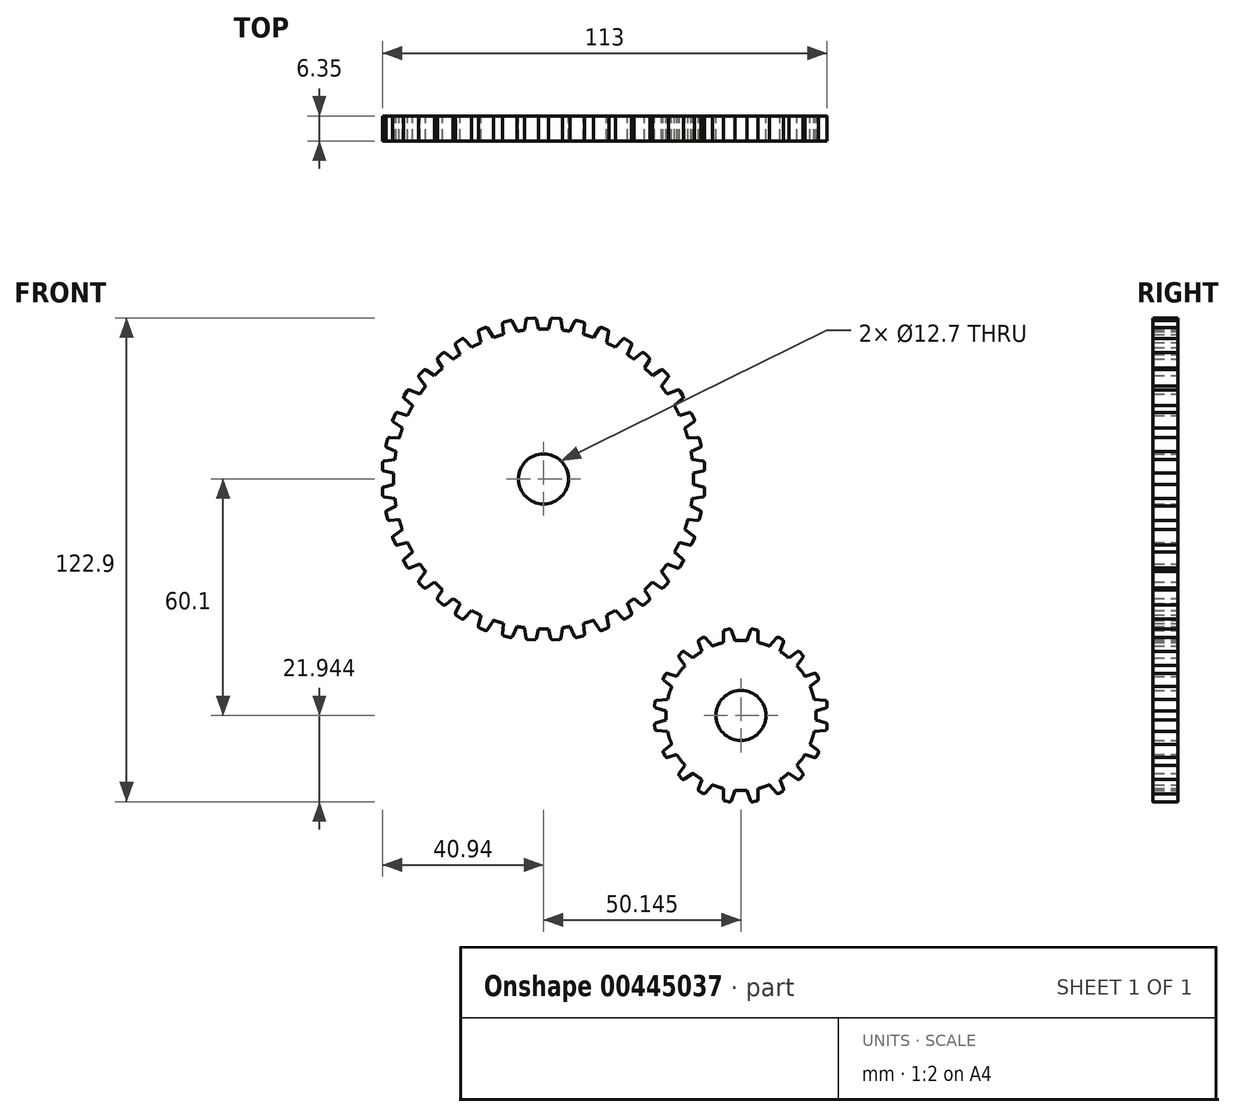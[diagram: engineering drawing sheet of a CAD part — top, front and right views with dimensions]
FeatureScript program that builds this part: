
annotation { "Feature Type Name" : "Feature", "Feature Type Description" : "" }
export const myFeature = defineFeature(function(context is Context, id is Id, definition is map)
    precondition{}
    {
        {
            var Q0;
            Q0=qCreatedBy(makeId("Front.planeOp"),FACE);
            var sketch = newSketch(context, id + "F0", { "sketchPlane" : qUnion([Q0])});
            skCircle(sketch, "E0", {"center": v(-27.1, 27.65) * mm, "radius": 38.1 * mm});
            skCircle(sketch, "E1", {"center": v(-27.1, 27.65) * mm, "radius": 6.35 * mm});
            skLineSegment(sketch, "E2", {"start": v(10.04, 32.06) * mm, "end": v(10.15, 29.52) * mm});
            skLineSegment(sketch, "E3", {"start": v(13.33, 32.24) * mm, "end": v(10.6, 32.59) * mm});
            skLineSegment(sketch, "E4", {"start": v(10.77, 29.05) * mm, "end": v(13.45, 29.65) * mm});
            skLineSegment(sketch, "E5", {"start": v(13.77, 31.76) * mm, "end": v(13.84, 30.17) * mm});
            skPoint(sketch, "E6.visualSharp", {"position": v(13.75, 32.18) * mm});
            skArc(sketch, "E6.filletArc", {"start": v(13.77, 31.76) * mm, "mid": v(13.64, 32.08) * mm, "end": v(13.33, 32.24) * mm});
            skPoint(sketch, "E7.visualSharp", {"position": v(10, 32.67) * mm});
            skArc(sketch, "E7.filletArc", {"start": v(10.6, 32.59) * mm, "mid": v(10.2, 32.46) * mm, "end": v(10.04, 32.06) * mm});
            skArc(sketch, "E8.filletArc", {"start": v(10.15, 29.52) * mm, "mid": v(10.35, 29.14) * mm, "end": v(10.77, 29.05) * mm});
            skPoint(sketch, "E9.visualSharp", {"position": v(13.86, 29.75) * mm});
            skArc(sketch, "E9.filletArc", {"start": v(13.45, 29.65) * mm, "mid": v(13.74, 29.84) * mm, "end": v(13.84, 30.17) * mm});
            skLineSegment(sketch, "E10.0", {"start": v(13.86, 29.75) * mm, "end": v(13.75, 32.18) * mm, "construction": true});
            skLineSegment(sketch, "E11", {"start": v(6.96, 43.07) * mm, "end": v(8.03, 40.77) * mm});
            skLineSegment(sketch, "E12", {"start": v(9.93, 44.48) * mm, "end": v(7.28, 43.77) * mm});
            skLineSegment(sketch, "E13", {"start": v(8.78, 40.57) * mm, "end": v(11.03, 42.14) * mm});
            skLineSegment(sketch, "E14", {"start": v(10.52, 44.2) * mm, "end": v(11.2, 42.77) * mm});
            skPoint(sketch, "E15.visualSharp", {"position": v(10.34, 44.6) * mm});
            skArc(sketch, "E15.filletArc", {"start": v(10.52, 44.2) * mm, "mid": v(10.28, 44.45) * mm, "end": v(9.93, 44.48) * mm});
            skPoint(sketch, "E16.visualSharp", {"position": v(6.7, 43.62) * mm});
            skArc(sketch, "E16.filletArc", {"start": v(7.28, 43.77) * mm, "mid": v(6.96, 43.5) * mm, "end": v(6.96, 43.07) * mm});
            skPoint(sketch, "E17.visualSharp", {"position": v(8.29, 40.22) * mm});
            skArc(sketch, "E17.filletArc", {"start": v(8.03, 40.77) * mm, "mid": v(8.36, 40.5) * mm, "end": v(8.78, 40.57) * mm});
            skPoint(sketch, "E18.visualSharp", {"position": v(11.38, 42.38) * mm});
            skArc(sketch, "E18.filletArc", {"start": v(11.03, 42.14) * mm, "mid": v(11.23, 42.42) * mm, "end": v(11.2, 42.77) * mm});
            skLineSegment(sketch, "E19.0", {"start": v(11.38, 42.38) * mm, "end": v(10.34, 44.6) * mm, "construction": true});
            skLineSegment(sketch, "E20", {"start": v(4.05, 48.5) * mm, "end": v(5.33, 46.32) * mm});
            skLineSegment(sketch, "E21", {"start": v(6.97, 50.23) * mm, "end": v(4.3, 49.24) * mm});
            skLineSegment(sketch, "E22", {"start": v(6.1, 46.19) * mm, "end": v(8.26, 48.02) * mm});
            skLineSegment(sketch, "E23", {"start": v(7.58, 50) * mm, "end": v(8.37, 48.67) * mm});
            skPoint(sketch, "E24.visualSharp", {"position": v(7.37, 50.38) * mm});
            skArc(sketch, "E24.filletArc", {"start": v(7.58, 50) * mm, "mid": v(7.32, 50.23) * mm, "end": v(6.97, 50.23) * mm});
            skPoint(sketch, "E25.visualSharp", {"position": v(3.74, 49.03) * mm});
            skArc(sketch, "E25.filletArc", {"start": v(4.3, 49.24) * mm, "mid": v(4, 48.94) * mm, "end": v(4.05, 48.5) * mm});
            skPoint(sketch, "E26.visualSharp", {"position": v(5.63, 45.8) * mm});
            skArc(sketch, "E26.filletArc", {"start": v(5.33, 46.32) * mm, "mid": v(5.68, 46.07) * mm, "end": v(6.1, 46.19) * mm});
            skPoint(sketch, "E27.visualSharp", {"position": v(8.58, 48.3) * mm});
            skArc(sketch, "E27.filletArc", {"start": v(8.26, 48.02) * mm, "mid": v(8.43, 48.32) * mm, "end": v(8.37, 48.67) * mm});
            skLineSegment(sketch, "E28.0", {"start": v(8.58, 48.3) * mm, "end": v(7.37, 50.38) * mm, "construction": true});
            skLineSegment(sketch, "E29", {"start": v(0.34, 53.06) * mm, "end": v(2.06, 51.19) * mm});
            skLineSegment(sketch, "E30", {"start": v(2.75, 55.3) * mm, "end": v(0.44, 53.83) * mm});
            skLineSegment(sketch, "E31", {"start": v(2.84, 51.22) * mm, "end": v(4.5, 53.4) * mm});
            skLineSegment(sketch, "E32", {"start": v(3.4, 55.22) * mm, "end": v(4.47, 54.06) * mm});
            skPoint(sketch, "E33.visualSharp", {"position": v(3.1, 55.54) * mm});
            skArc(sketch, "E33.filletArc", {"start": v(3.4, 55.22) * mm, "mid": v(3.09, 55.38) * mm, "end": v(2.75, 55.3) * mm});
            skPoint(sketch, "E34.visualSharp", {"position": v(-0.07, 53.5) * mm});
            skArc(sketch, "E34.filletArc", {"start": v(0.44, 53.83) * mm, "mid": v(0.2, 53.47) * mm, "end": v(0.34, 53.06) * mm});
            skPoint(sketch, "E35.visualSharp", {"position": v(2.47, 50.74) * mm});
            skArc(sketch, "E35.filletArc", {"start": v(2.06, 51.19) * mm, "mid": v(2.46, 51.03) * mm, "end": v(2.84, 51.22) * mm});
            skPoint(sketch, "E36.visualSharp", {"position": v(4.76, 53.74) * mm});
            skArc(sketch, "E36.filletArc", {"start": v(4.5, 53.4) * mm, "mid": v(4.6, 53.74) * mm, "end": v(4.47, 54.06) * mm});
            skLineSegment(sketch, "E37.0", {"start": v(4.76, 53.74) * mm, "end": v(3.1, 55.54) * mm, "construction": true});
            skLineSegment(sketch, "E38", {"start": v(-8.73, 60.35) * mm, "end": v(-6.6, 58.97) * mm});
            skLineSegment(sketch, "E39", {"start": v(-6.96, 63.13) * mm, "end": v(-8.82, 61.12) * mm});
            skLineSegment(sketch, "E40", {"start": v(-5.85, 59.2) * mm, "end": v(-4.79, 61.73) * mm});
            skLineSegment(sketch, "E41", {"start": v(-6.31, 63.21) * mm, "end": v(-4.98, 62.35) * mm});
            skPoint(sketch, "E42.visualSharp", {"position": v(-6.67, 63.44) * mm});
            skArc(sketch, "E42.filletArc", {"start": v(-6.31, 63.21) * mm, "mid": v(-6.65, 63.29) * mm, "end": v(-6.96, 63.13) * mm});
            skPoint(sketch, "E43.visualSharp", {"position": v(-9.24, 60.68) * mm});
            skArc(sketch, "E43.filletArc", {"start": v(-8.82, 61.12) * mm, "mid": v(-8.96, 60.71) * mm, "end": v(-8.73, 60.35) * mm});
            skPoint(sketch, "E44.visualSharp", {"position": v(-6.09, 58.64) * mm});
            skArc(sketch, "E44.filletArc", {"start": v(-6.6, 58.97) * mm, "mid": v(-6.17, 58.91) * mm, "end": v(-5.85, 59.2) * mm});
            skPoint(sketch, "E45.visualSharp", {"position": v(-4.62, 62.12) * mm});
            skArc(sketch, "E45.filletArc", {"start": v(-4.79, 61.73) * mm, "mid": v(-4.77, 62.07) * mm, "end": v(-4.98, 62.35) * mm});
            skLineSegment(sketch, "E46.0", {"start": v(-4.62, 62.12) * mm, "end": v(-6.67, 63.44) * mm, "construction": true});
            skLineSegment(sketch, "E47", {"start": v(-14.2, 62.88) * mm, "end": v(-11.86, 61.89) * mm});
            skLineSegment(sketch, "E48", {"start": v(-12.92, 65.94) * mm, "end": v(-14.42, 63.62) * mm});
            skLineSegment(sketch, "E49", {"start": v(-11.16, 62.24) * mm, "end": v(-10.54, 64.93) * mm});
            skLineSegment(sketch, "E50", {"start": v(-12.3, 66.13) * mm, "end": v(-10.84, 65.51) * mm});
            skPoint(sketch, "E51.visualSharp", {"position": v(-12.69, 66.3) * mm});
            skArc(sketch, "E51.filletArc", {"start": v(-12.3, 66.13) * mm, "mid": v(-12.64, 66.15) * mm, "end": v(-12.92, 65.94) * mm});
            skPoint(sketch, "E52.visualSharp", {"position": v(-14.75, 63.12) * mm});
            skArc(sketch, "E52.filletArc", {"start": v(-14.42, 63.62) * mm, "mid": v(-14.48, 63.2) * mm, "end": v(-14.2, 62.88) * mm});
            skPoint(sketch, "E53.visualSharp", {"position": v(-11.3, 61.65) * mm});
            skArc(sketch, "E53.filletArc", {"start": v(-11.86, 61.89) * mm, "mid": v(-11.43, 61.9) * mm, "end": v(-11.16, 62.24) * mm});
            skPoint(sketch, "E54.visualSharp", {"position": v(-10.45, 65.34) * mm});
            skArc(sketch, "E54.filletArc", {"start": v(-10.54, 64.93) * mm, "mid": v(-10.59, 65.27) * mm, "end": v(-10.84, 65.51) * mm});
            skLineSegment(sketch, "E55.0", {"start": v(-10.45, 65.34) * mm, "end": v(-12.69, 66.3) * mm, "construction": true});
            skLineSegment(sketch, "E56", {"start": v(-20.02, 64.46) * mm, "end": v(-17.57, 63.8) * mm});
            skLineSegment(sketch, "E57", {"start": v(-19.2, 67.65) * mm, "end": v(-20.35, 65.17) * mm});
            skLineSegment(sketch, "E58", {"start": v(-16.93, 64.25) * mm, "end": v(-16.7, 66.98) * mm});
            skLineSegment(sketch, "E59", {"start": v(-18.6, 67.93) * mm, "end": v(-17.07, 67.52) * mm});
            skPoint(sketch, "E60.visualSharp", {"position": v(-19.02, 68.04) * mm});
            skArc(sketch, "E60.filletArc", {"start": v(-18.6, 67.93) * mm, "mid": v(-18.95, 67.9) * mm, "end": v(-19.2, 67.65) * mm});
            skPoint(sketch, "E61.visualSharp", {"position": v(-20.6, 64.62) * mm});
            skArc(sketch, "E61.filletArc", {"start": v(-20.35, 65.17) * mm, "mid": v(-20.35, 64.74) * mm, "end": v(-20.02, 64.46) * mm});
            skPoint(sketch, "E62.visualSharp", {"position": v(-16.98, 63.65) * mm});
            skArc(sketch, "E62.filletArc", {"start": v(-17.57, 63.8) * mm, "mid": v(-17.15, 63.88) * mm, "end": v(-16.93, 64.25) * mm});
            skPoint(sketch, "E63.visualSharp", {"position": v(-16.66, 67.4) * mm});
            skArc(sketch, "E63.filletArc", {"start": v(-16.7, 66.98) * mm, "mid": v(-16.79, 67.32) * mm, "end": v(-17.07, 67.52) * mm});
            skLineSegment(sketch, "E64.0", {"start": v(-16.66, 67.4) * mm, "end": v(-19.02, 68.04) * mm, "construction": true});
            skLineSegment(sketch, "E65", {"start": v(8.98, 37.34) * mm, "end": v(9.63, 34.89) * mm});
            skLineSegment(sketch, "E66", {"start": v(11.97, 38.2) * mm, "end": v(9.42, 37.98) * mm});
            skLineSegment(sketch, "E67", {"start": v(10.34, 34.56) * mm, "end": v(12.66, 35.63) * mm});
            skLineSegment(sketch, "E68", {"start": v(12.5, 37.82) * mm, "end": v(12.93, 36.22) * mm});
            skPoint(sketch, "E69.visualSharp", {"position": v(12.4, 38.23) * mm});
            skArc(sketch, "E69.filletArc", {"start": v(12.5, 37.82) * mm, "mid": v(12.3, 38.1) * mm, "end": v(11.97, 38.2) * mm});
            skPoint(sketch, "E70.visualSharp", {"position": v(8.82, 37.92) * mm});
            skArc(sketch, "E70.filletArc", {"start": v(9.42, 37.98) * mm, "mid": v(9.05, 37.76) * mm, "end": v(8.98, 37.34) * mm});
            skPoint(sketch, "E71.visualSharp", {"position": v(9.79, 34.3) * mm});
            skArc(sketch, "E71.filletArc", {"start": v(9.63, 34.89) * mm, "mid": v(9.9, 34.56) * mm, "end": v(10.34, 34.56) * mm});
            skPoint(sketch, "E72.visualSharp", {"position": v(13.04, 35.81) * mm});
            skArc(sketch, "E72.filletArc", {"start": v(12.66, 35.63) * mm, "mid": v(12.9, 35.88) * mm, "end": v(12.93, 36.22) * mm});
            skLineSegment(sketch, "E73.0", {"start": v(13.04, 35.81) * mm, "end": v(12.4, 38.23) * mm, "construction": true});
            skLineSegment(sketch, "E74", {"start": v(-25.32, 65) * mm, "end": v(-22.78, 64.91) * mm});
            skLineSegment(sketch, "E75", {"start": v(-25.27, 68.11) * mm, "end": v(-25.8, 65.6) * mm});
            skLineSegment(sketch, "E76", {"start": v(-22.26, 65.49) * mm, "end": v(-22.62, 68.02) * mm});
            skLineSegment(sketch, "E77", {"start": v(-24.76, 68.51) * mm, "end": v(-23.1, 68.46) * mm});
            skPoint(sketch, "E78.visualSharp", {"position": v(-25.18, 68.53) * mm});
            skArc(sketch, "E78.filletArc", {"start": v(-24.76, 68.51) * mm, "mid": v(-25.09, 68.4) * mm, "end": v(-25.27, 68.11) * mm});
            skPoint(sketch, "E79.visualSharp", {"position": v(-25.93, 65.02) * mm});
            skArc(sketch, "E79.filletArc", {"start": v(-25.8, 65.6) * mm, "mid": v(-25.7, 65.2) * mm, "end": v(-25.32, 65) * mm});
            skPoint(sketch, "E80.visualSharp", {"position": v(-22.18, 64.9) * mm});
            skArc(sketch, "E80.filletArc", {"start": v(-22.78, 64.91) * mm, "mid": v(-22.39, 65.08) * mm, "end": v(-22.26, 65.49) * mm});
            skPoint(sketch, "E81.visualSharp", {"position": v(-22.68, 68.44) * mm});
            skArc(sketch, "E81.filletArc", {"start": v(-22.62, 68.02) * mm, "mid": v(-22.79, 68.33) * mm, "end": v(-23.1, 68.46) * mm});
            skLineSegment(sketch, "E82.0", {"start": v(-22.68, 68.44) * mm, "end": v(-25.18, 68.53) * mm, "construction": true});
            skPoint(sketch, "E83.endSnap0", {"position": v(10.7, 38.09) * mm});
            skLineSegment(sketch, "E84", {"start": v(-27.1, 65.75) * mm, "end": v(-27.1, -10.45) * mm, "construction": true});
            skLineSegment(sketch, "E85", {"start": v(-65.2, 27.65) * mm, "end": v(11, 27.65) * mm, "construction": true});
            skLineSegment(sketch, "E86", {"start": v(-4.21, 57.29) * mm, "end": v(-2.34, 55.57) * mm});
            skLineSegment(sketch, "E87", {"start": v(-2.15, 59.62) * mm, "end": v(-4.18, 58.06) * mm});
            skLineSegment(sketch, "E88", {"start": v(-1.57, 55.68) * mm, "end": v(-0.2, 57.84) * mm});
            skLineSegment(sketch, "E89", {"start": v(-1.5, 59.6) * mm, "end": v(-0.28, 58.48) * mm});
            skPoint(sketch, "E90.visualSharp", {"position": v(-1.82, 59.88) * mm});
            skArc(sketch, "E90.filletArc", {"start": v(-1.5, 59.6) * mm, "mid": v(-1.82, 59.73) * mm, "end": v(-2.15, 59.62) * mm});
            skPoint(sketch, "E91.visualSharp", {"position": v(-4.66, 57.7) * mm});
            skArc(sketch, "E91.filletArc", {"start": v(-4.18, 58.06) * mm, "mid": v(-4.38, 57.68) * mm, "end": v(-4.21, 57.29) * mm});
            skPoint(sketch, "E92.visualSharp", {"position": v(-1.9, 55.16) * mm});
            skArc(sketch, "E92.filletArc", {"start": v(-2.34, 55.57) * mm, "mid": v(-1.93, 55.44) * mm, "end": v(-1.57, 55.68) * mm});
            skPoint(sketch, "E93.visualSharp", {"position": v(0.03, 58.2) * mm});
            skArc(sketch, "E93.filletArc", {"start": v(-0.2, 57.84) * mm, "mid": v(-0.12, 58.17) * mm, "end": v(-0.28, 58.48) * mm});
            skLineSegment(sketch, "E94.0", {"start": v(0.03, 58.2) * mm, "end": v(-1.82, 59.88) * mm, "construction": true});
            skLineSegment(sketch, "E95.MirrorCS", {"start": v(-57.6, 55.22) * mm, "end": v(-58.67, 54.06) * mm});
            skArc(sketch, "E96.MirrorCS", {"start": v(-29.44, 68.51) * mm, "mid": v(-29.11, 68.4) * mm, "end": v(-28.93, 68.11) * mm});
            skArc(sketch, "E97.MirrorCS", {"start": v(-37.5, 66.98) * mm, "mid": v(-37.41, 67.32) * mm, "end": v(-37.13, 67.52) * mm});
            skLineSegment(sketch, "E98.MirrorCS", {"start": v(-61.78, 50) * mm, "end": v(-62.57, 48.67) * mm});
            skArc(sketch, "E99.MirrorCS", {"start": v(-66.7, 37.82) * mm, "mid": v(-66.5, 38.1) * mm, "end": v(-66.17, 38.2) * mm});
            skArc(sketch, "E100.MirrorCS", {"start": v(-43.66, 64.93) * mm, "mid": v(-43.61, 65.27) * mm, "end": v(-43.36, 65.51) * mm});
            skArc(sketch, "E101.MirrorCS", {"start": v(-63.62, 37.98) * mm, "mid": v(-63.25, 37.76) * mm, "end": v(-63.18, 37.34) * mm});
            skArc(sketch, "E102.MirrorCS", {"start": v(-33.85, 65.17) * mm, "mid": v(-33.85, 64.74) * mm, "end": v(-34.18, 64.46) * mm});
            skArc(sketch, "E103.MirrorCS", {"start": v(-49.42, 61.73) * mm, "mid": v(-49.43, 62.07) * mm, "end": v(-49.22, 62.35) * mm});
            skArc(sketch, "E104.MirrorCS", {"start": v(-64.8, 32.59) * mm, "mid": v(-64.4, 32.46) * mm, "end": v(-64.24, 32.06) * mm});
            skArc(sketch, "E105.MirrorCS", {"start": v(-50.02, 58.06) * mm, "mid": v(-49.82, 57.68) * mm, "end": v(-49.99, 57.29) * mm});
            skArc(sketch, "E106.MirrorCS", {"start": v(-66.86, 35.63) * mm, "mid": v(-67.1, 35.88) * mm, "end": v(-67.13, 36.22) * mm});
            skArc(sketch, "E107.MirrorCS", {"start": v(-54.64, 53.83) * mm, "mid": v(-54.4, 53.47) * mm, "end": v(-54.54, 53.06) * mm});
            skLineSegment(sketch, "E108.MirrorCS", {"start": v(-49.58, 62.12) * mm, "end": v(-47.53, 63.44) * mm, "construction": true});
            skArc(sketch, "E109.MirrorCS", {"start": v(-31.58, 68.02) * mm, "mid": v(-31.41, 68.33) * mm, "end": v(-31.1, 68.46) * mm});
            skArc(sketch, "E110.MirrorCS", {"start": v(-36.63, 63.8) * mm, "mid": v(-37.05, 63.88) * mm, "end": v(-37.27, 64.25) * mm});
            skArc(sketch, "E111.MirrorCS", {"start": v(-62.23, 40.77) * mm, "mid": v(-62.56, 40.5) * mm, "end": v(-62.98, 40.57) * mm});
            skLineSegment(sketch, "E112.MirrorCS", {"start": v(-43.75, 65.34) * mm, "end": v(-41.51, 66.3) * mm, "construction": true});
            skArc(sketch, "E113.MirrorCS", {"start": v(-39.78, 63.62) * mm, "mid": v(-39.72, 63.2) * mm, "end": v(-40, 62.88) * mm});
            skArc(sketch, "E114.MirrorCS", {"start": v(-31.42, 64.91) * mm, "mid": v(-31.81, 65.08) * mm, "end": v(-31.94, 65.49) * mm});
            skArc(sketch, "E115.MirrorCS", {"start": v(-62.46, 48.02) * mm, "mid": v(-62.63, 48.32) * mm, "end": v(-62.57, 48.67) * mm});
            skArc(sketch, "E116.MirrorCS", {"start": v(-64.35, 29.52) * mm, "mid": v(-64.55, 29.14) * mm, "end": v(-64.97, 29.05) * mm});
            skLineSegment(sketch, "E117.MirrorCS", {"start": v(-41.9, 66.13) * mm, "end": v(-43.36, 65.51) * mm});
            skArc(sketch, "E118.MirrorCS", {"start": v(-58.5, 49.24) * mm, "mid": v(-58.2, 48.94) * mm, "end": v(-58.25, 48.5) * mm});
            skArc(sketch, "E119.MirrorCS", {"start": v(-47.6, 58.97) * mm, "mid": v(-48.03, 58.91) * mm, "end": v(-48.35, 59.2) * mm});
            skArc(sketch, "E120.MirrorCS", {"start": v(-35.6, 67.93) * mm, "mid": v(-35.25, 67.9) * mm, "end": v(-35, 67.65) * mm});
            skLineSegment(sketch, "E121.MirrorCS", {"start": v(-47.89, 63.21) * mm, "end": v(-49.22, 62.35) * mm});
            skArc(sketch, "E122.MirrorCS", {"start": v(-67.97, 31.76) * mm, "mid": v(-67.84, 32.08) * mm, "end": v(-67.53, 32.24) * mm});
            skArc(sketch, "E123.MirrorCS", {"start": v(-59.53, 46.32) * mm, "mid": v(-59.88, 46.07) * mm, "end": v(-60.3, 46.19) * mm});
            skArc(sketch, "E124.MirrorCS", {"start": v(-47.89, 63.21) * mm, "mid": v(-47.55, 63.29) * mm, "end": v(-47.24, 63.13) * mm});
            skLineSegment(sketch, "E125.MirrorCS", {"start": v(-58.96, 53.74) * mm, "end": v(-57.3, 55.54) * mm, "construction": true});
            skArc(sketch, "E126.MirrorCS", {"start": v(-63.83, 34.89) * mm, "mid": v(-64.1, 34.56) * mm, "end": v(-64.54, 34.56) * mm});
            skLineSegment(sketch, "E127.MirrorCS", {"start": v(-62.78, 48.3) * mm, "end": v(-61.57, 50.38) * mm, "construction": true});
            skArc(sketch, "E128.MirrorCS", {"start": v(-51.86, 55.57) * mm, "mid": v(-52.27, 55.44) * mm, "end": v(-52.63, 55.68) * mm});
            skArc(sketch, "E129.MirrorCS", {"start": v(-64.73, 44.2) * mm, "mid": v(-64.48, 44.45) * mm, "end": v(-64.13, 44.48) * mm});
            skArc(sketch, "E130.MirrorCS", {"start": v(-54, 57.84) * mm, "mid": v(-54.08, 58.17) * mm, "end": v(-53.92, 58.48) * mm});
            skArc(sketch, "E131.MirrorCS", {"start": v(-61.78, 50) * mm, "mid": v(-61.52, 50.23) * mm, "end": v(-61.17, 50.23) * mm});
            skArc(sketch, "E132.MirrorCS", {"start": v(-45.38, 61.12) * mm, "mid": v(-45.24, 60.71) * mm, "end": v(-45.47, 60.35) * mm});
            skArc(sketch, "E133.MirrorCS", {"start": v(-58.7, 53.4) * mm, "mid": v(-58.8, 53.74) * mm, "end": v(-58.67, 54.06) * mm});
            skArc(sketch, "E134.MirrorCS", {"start": v(-52.7, 59.6) * mm, "mid": v(-52.38, 59.73) * mm, "end": v(-52.05, 59.62) * mm});
            skArc(sketch, "E135.MirrorCS", {"start": v(-56.26, 51.19) * mm, "mid": v(-56.66, 51.03) * mm, "end": v(-57.04, 51.22) * mm});
            skArc(sketch, "E136.MirrorCS", {"start": v(-42.34, 61.89) * mm, "mid": v(-42.77, 61.9) * mm, "end": v(-43.04, 62.24) * mm});
            skArc(sketch, "E137.MirrorCS", {"start": v(-65.23, 42.14) * mm, "mid": v(-65.43, 42.42) * mm, "end": v(-65.4, 42.77) * mm});
            skArc(sketch, "E138.MirrorCS", {"start": v(-57.6, 55.22) * mm, "mid": v(-57.29, 55.38) * mm, "end": v(-56.95, 55.3) * mm});
            skArc(sketch, "E139.MirrorCS", {"start": v(-61.49, 43.77) * mm, "mid": v(-61.16, 43.5) * mm, "end": v(-61.16, 43.07) * mm});
            skArc(sketch, "E140.MirrorCS", {"start": v(-28.4, 65.6) * mm, "mid": v(-28.5, 65.2) * mm, "end": v(-28.88, 65) * mm});
            skArc(sketch, "E141.MirrorCS", {"start": v(-41.9, 66.13) * mm, "mid": v(-41.56, 66.15) * mm, "end": v(-41.28, 65.94) * mm});
            skLineSegment(sketch, "E142.MirrorCS", {"start": v(-29.44, 68.51) * mm, "end": v(-31.1, 68.46) * mm});
            skLineSegment(sketch, "E143.MirrorCS", {"start": v(-52.7, 59.6) * mm, "end": v(-53.92, 58.48) * mm});
            skLineSegment(sketch, "E144.MirrorCS", {"start": v(-64.73, 44.2) * mm, "end": v(-65.4, 42.77) * mm});
            skLineSegment(sketch, "E145.MirrorCS", {"start": v(-66.7, 37.82) * mm, "end": v(-67.13, 36.22) * mm});
            skLineSegment(sketch, "E146.MirrorCS", {"start": v(-35.6, 67.93) * mm, "end": v(-37.13, 67.52) * mm});
            skLineSegment(sketch, "E147.MirrorCS", {"start": v(-66.17, 38.2) * mm, "end": v(-63.62, 37.98) * mm});
            skArc(sketch, "E148.MirrorCS", {"start": v(-67.65, 29.65) * mm, "mid": v(-67.94, 29.84) * mm, "end": v(-68.04, 30.17) * mm});
            skLineSegment(sketch, "E149.MirrorCS", {"start": v(-54.23, 58.2) * mm, "end": v(-52.38, 59.88) * mm, "construction": true});
            skLineSegment(sketch, "E150.MirrorCS", {"start": v(-28.88, 65) * mm, "end": v(-31.42, 64.91) * mm});
            skLineSegment(sketch, "E151.MirrorCS", {"start": v(-37.54, 67.4) * mm, "end": v(-35.18, 68.04) * mm, "construction": true});
            skLineSegment(sketch, "E152.MirrorCS", {"start": v(-31.52, 68.44) * mm, "end": v(-29.02, 68.53) * mm, "construction": true});
            skLineSegment(sketch, "E153.MirrorCS", {"start": v(-61.16, 43.07) * mm, "end": v(-62.23, 40.77) * mm});
            skLineSegment(sketch, "E154.MirrorCS", {"start": v(-67.97, 31.76) * mm, "end": v(-68.04, 30.17) * mm});
            skLineSegment(sketch, "E155.MirrorCS", {"start": v(-67.24, 35.81) * mm, "end": v(-66.6, 38.23) * mm, "construction": true});
            skLineSegment(sketch, "E156.MirrorCS", {"start": v(-40, 62.88) * mm, "end": v(-42.34, 61.89) * mm});
            skLineSegment(sketch, "E157.MirrorCS", {"start": v(-65.58, 42.38) * mm, "end": v(-64.55, 44.6) * mm, "construction": true});
            skLineSegment(sketch, "E158.MirrorCS", {"start": v(-34.18, 64.46) * mm, "end": v(-36.63, 63.8) * mm});
            skLineSegment(sketch, "E159.MirrorCS", {"start": v(-52.05, 59.62) * mm, "end": v(-50.02, 58.06) * mm});
            skPoint(sketch, "E160.MirrorP", {"position": v(-52.38, 59.88) * mm});
            skPoint(sketch, "E161.MirrorP", {"position": v(-47.53, 63.44) * mm});
            skLineSegment(sketch, "E162.MirrorCS", {"start": v(-52.63, 55.68) * mm, "end": v(-54, 57.84) * mm});
            skLineSegment(sketch, "E163.MirrorCS", {"start": v(-60.3, 46.19) * mm, "end": v(-62.46, 48.02) * mm});
            skPoint(sketch, "E164.MirrorP", {"position": v(-67.24, 35.81) * mm});
            skLineSegment(sketch, "E165.MirrorCS", {"start": v(-41.28, 65.94) * mm, "end": v(-39.78, 63.62) * mm});
            skPoint(sketch, "E166.MirrorP", {"position": v(-49.58, 62.12) * mm});
            skPoint(sketch, "E167.MirrorP", {"position": v(-62.78, 48.3) * mm});
            skLineSegment(sketch, "E168.MirrorCS", {"start": v(-54.54, 53.06) * mm, "end": v(-56.26, 51.19) * mm});
            skPoint(sketch, "E169.MirrorP", {"position": v(-31.52, 68.44) * mm});
            skPoint(sketch, "E170.MirrorP", {"position": v(-37.54, 67.4) * mm});
            skLineSegment(sketch, "E171.MirrorCS", {"start": v(-43.04, 62.24) * mm, "end": v(-43.66, 64.93) * mm});
            skLineSegment(sketch, "E172.MirrorCS", {"start": v(-37.27, 64.25) * mm, "end": v(-37.5, 66.98) * mm});
            skPoint(sketch, "E173.MirrorP", {"position": v(-37.22, 63.65) * mm});
            skLineSegment(sketch, "E174.MirrorCS", {"start": v(-56.95, 55.3) * mm, "end": v(-54.64, 53.83) * mm});
            skPoint(sketch, "E175.MirrorP", {"position": v(-64.55, 44.6) * mm});
            skPoint(sketch, "E176.MirrorP", {"position": v(-58.96, 53.74) * mm});
            skLineSegment(sketch, "E177.MirrorCS", {"start": v(-64.97, 29.05) * mm, "end": v(-67.65, 29.65) * mm});
            skLineSegment(sketch, "E178.MirrorCS", {"start": v(-31.94, 65.49) * mm, "end": v(-31.58, 68.02) * mm});
            skPoint(sketch, "E179.MirrorP", {"position": v(-63.02, 37.92) * mm});
            skPoint(sketch, "E180.MirrorP", {"position": v(-57.94, 49.03) * mm});
            skLineSegment(sketch, "E181.MirrorCS", {"start": v(-63.18, 37.34) * mm, "end": v(-63.83, 34.89) * mm});
            skLineSegment(sketch, "E182.MirrorCS", {"start": v(-62.98, 40.57) * mm, "end": v(-65.23, 42.14) * mm});
            skLineSegment(sketch, "E183.MirrorCS", {"start": v(-67.53, 32.24) * mm, "end": v(-64.8, 32.59) * mm});
            skLineSegment(sketch, "E184.MirrorCS", {"start": v(-57.04, 51.22) * mm, "end": v(-58.7, 53.4) * mm});
            skPoint(sketch, "E185.MirrorP", {"position": v(-52.3, 55.16) * mm});
            skPoint(sketch, "E186.MirrorP", {"position": v(-32.02, 64.9) * mm});
            skLineSegment(sketch, "E187.MirrorCS", {"start": v(-64.54, 34.56) * mm, "end": v(-66.86, 35.63) * mm});
            skPoint(sketch, "E188.MirrorP", {"position": v(-59.83, 45.8) * mm});
            skLineSegment(sketch, "E189.MirrorCS", {"start": v(-64.24, 32.06) * mm, "end": v(-64.35, 29.52) * mm});
            skPoint(sketch, "E190.MirrorP", {"position": v(-39.45, 63.12) * mm});
            skPoint(sketch, "E191.MirrorP", {"position": v(-61.57, 50.38) * mm});
            skPoint(sketch, "E192.MirrorP", {"position": v(-48.12, 58.64) * mm});
            skPoint(sketch, "E193.MirrorP", {"position": v(-64.9, 38.09) * mm});
            skPoint(sketch, "E194.MirrorP", {"position": v(-49.54, 57.7) * mm});
            skPoint(sketch, "E195.MirrorP", {"position": v(-66.6, 38.23) * mm});
            skPoint(sketch, "E196.MirrorP", {"position": v(-54.13, 53.5) * mm});
            skPoint(sketch, "E197.MirrorP", {"position": v(-54.23, 58.2) * mm});
            skPoint(sketch, "E198.MirrorP", {"position": v(-60.9, 43.62) * mm});
            skPoint(sketch, "E199.MirrorP", {"position": v(-64.2, 32.67) * mm});
            skLineSegment(sketch, "E200.MirrorCS", {"start": v(-28.93, 68.11) * mm, "end": v(-28.4, 65.6) * mm});
            skPoint(sketch, "E201.MirrorP", {"position": v(-33.6, 64.62) * mm});
            skLineSegment(sketch, "E202.MirrorCS", {"start": v(-45.47, 60.35) * mm, "end": v(-47.6, 58.97) * mm});
            skLineSegment(sketch, "E203.MirrorCS", {"start": v(-68.06, 29.75) * mm, "end": v(-67.95, 32.18) * mm, "construction": true});
            skPoint(sketch, "E204.MirrorP", {"position": v(-28.27, 65.02) * mm});
            skLineSegment(sketch, "E205.MirrorCS", {"start": v(-64.13, 44.48) * mm, "end": v(-61.49, 43.77) * mm});
            skLineSegment(sketch, "E206.MirrorCS", {"start": v(-35, 67.65) * mm, "end": v(-33.85, 65.17) * mm});
            skPoint(sketch, "E207.MirrorP", {"position": v(-44.96, 60.68) * mm});
            skLineSegment(sketch, "E208.MirrorCS", {"start": v(-47.24, 63.13) * mm, "end": v(-45.38, 61.12) * mm});
            skLineSegment(sketch, "E209.MirrorCS", {"start": v(-61.17, 50.23) * mm, "end": v(-58.5, 49.24) * mm});
            skLineSegment(sketch, "E210.MirrorCS", {"start": v(-49.99, 57.29) * mm, "end": v(-51.86, 55.57) * mm});
            skPoint(sketch, "E211.MirrorP", {"position": v(-63.99, 34.3) * mm});
            skPoint(sketch, "E212.MirrorP", {"position": v(-35.18, 68.04) * mm});
            skLineSegment(sketch, "E213.MirrorCS", {"start": v(-48.35, 59.2) * mm, "end": v(-49.42, 61.73) * mm});
            skPoint(sketch, "E214.MirrorP", {"position": v(-29.02, 68.53) * mm});
            skPoint(sketch, "E215.MirrorP", {"position": v(-65.58, 42.38) * mm});
            skPoint(sketch, "E216.MirrorP", {"position": v(-56.67, 50.74) * mm});
            skPoint(sketch, "E217.MirrorP", {"position": v(-42.9, 61.65) * mm});
            skPoint(sketch, "E218.MirrorP", {"position": v(-41.51, 66.3) * mm});
            skPoint(sketch, "E219.MirrorP", {"position": v(-57.3, 55.54) * mm});
            skPoint(sketch, "E220.MirrorP", {"position": v(-62.49, 40.22) * mm});
            skPoint(sketch, "E221.MirrorP", {"position": v(-43.75, 65.34) * mm});
            skLineSegment(sketch, "E222.MirrorCS", {"start": v(-58.25, 48.5) * mm, "end": v(-59.53, 46.32) * mm});
            skPoint(sketch, "E223.MirrorP", {"position": v(-68.06, 29.75) * mm});
            skPoint(sketch, "E224.MirrorP", {"position": v(-67.95, 32.18) * mm});
            skLineSegment(sketch, "E225.MirrorCS", {"start": v(11, 27.65) * mm, "end": v(-65.2, 27.65) * mm, "construction": true});
            skLineSegment(sketch, "E226.MirrorCS", {"start": v(3.4, 0.08) * mm, "end": v(4.47, 1.25) * mm});
            skLineSegment(sketch, "E227.MirrorCS", {"start": v(-18.6, -12.62) * mm, "end": v(-17.07, -12.21) * mm});
            skLineSegment(sketch, "E228.MirrorCS", {"start": v(7.58, 5.3) * mm, "end": v(8.37, 6.64) * mm});
            skLineSegment(sketch, "E229.MirrorCS", {"start": v(-52.7, -4.29) * mm, "end": v(-53.92, -3.18) * mm});
            skArc(sketch, "E230.MirrorCS", {"start": v(7.58, 5.3) * mm, "mid": v(7.32, 5.08) * mm, "end": v(6.97, 5.08) * mm});
            skArc(sketch, "E231.MirrorCS", {"start": v(-12.3, -10.82) * mm, "mid": v(-12.64, -10.84) * mm, "end": v(-12.92, -10.63) * mm});
            skLineSegment(sketch, "E232.MirrorCS", {"start": v(4.76, 1.56) * mm, "end": v(3.1, -0.23) * mm, "construction": true});
            skLineSegment(sketch, "E233.MirrorCS", {"start": v(-6.31, -7.9) * mm, "end": v(-4.98, -7.04) * mm});
            skLineSegment(sketch, "E234.MirrorCS", {"start": v(12.5, 17.49) * mm, "end": v(12.93, 19.08) * mm});
            skArc(sketch, "E235.MirrorCS", {"start": v(4.5, 1.9) * mm, "mid": v(4.6, 1.57) * mm, "end": v(4.47, 1.25) * mm});
            skArc(sketch, "E236.MirrorCS", {"start": v(3.4, 0.08) * mm, "mid": v(3.09, -0.08) * mm, "end": v(2.75, 0) * mm});
            skLineSegment(sketch, "E237.MirrorCS", {"start": v(-24.76, -13.2) * mm, "end": v(-23.1, -13.15) * mm});
            skArc(sketch, "E238.MirrorCS", {"start": v(-16.7, -11.68) * mm, "mid": v(-16.79, -12.01) * mm, "end": v(-17.07, -12.21) * mm});
            skLineSegment(sketch, "E239.MirrorCS", {"start": v(-61.78, 5.3) * mm, "end": v(-62.57, 6.64) * mm});
            skArc(sketch, "E240.MirrorCS", {"start": v(-18.6, -12.62) * mm, "mid": v(-18.95, -12.6) * mm, "end": v(-19.2, -12.35) * mm});
            skArc(sketch, "E241.MirrorCS", {"start": v(-24.76, -13.2) * mm, "mid": v(-25.09, -13.1) * mm, "end": v(-25.27, -12.8) * mm});
            skLineSegment(sketch, "E242.MirrorCS", {"start": v(-41.9, -10.82) * mm, "end": v(-43.36, -10.2) * mm});
            skLineSegment(sketch, "E243.MirrorCS", {"start": v(-1.5, -4.29) * mm, "end": v(-0.28, -3.18) * mm});
            skArc(sketch, "E244.MirrorCS", {"start": v(12.5, 17.49) * mm, "mid": v(12.3, 17.2) * mm, "end": v(11.97, 17.11) * mm});
            skLineSegment(sketch, "E245.MirrorCS", {"start": v(-12.3, -10.82) * mm, "end": v(-10.84, -10.2) * mm});
            skArc(sketch, "E246.MirrorCS", {"start": v(-4.79, -6.42) * mm, "mid": v(-4.77, -6.77) * mm, "end": v(-4.98, -7.04) * mm});
            skArc(sketch, "E247.MirrorCS", {"start": v(-1.5, -4.29) * mm, "mid": v(-1.82, -4.42) * mm, "end": v(-2.15, -4.32) * mm});
            skLineSegment(sketch, "E248.MirrorCS", {"start": v(-35.6, -12.62) * mm, "end": v(-37.13, -12.21) * mm});
            skLineSegment(sketch, "E249.MirrorCS", {"start": v(-66.7, 17.49) * mm, "end": v(-67.13, 19.08) * mm});
            skArc(sketch, "E250.MirrorCS", {"start": v(-56.26, 4.12) * mm, "mid": v(-56.66, 4.28) * mm, "end": v(-57.04, 4.08) * mm});
            skLineSegment(sketch, "E251.MirrorCS", {"start": v(-43.75, -10.04) * mm, "end": v(-41.51, -10.99) * mm, "construction": true});
            skLineSegment(sketch, "E252.MirrorCS", {"start": v(-29.44, -13.2) * mm, "end": v(-31.1, -13.15) * mm});
            skArc(sketch, "E253.MirrorCS", {"start": v(-45.38, -5.81) * mm, "mid": v(-45.24, -5.4) * mm, "end": v(-45.47, -5.04) * mm});
            skLineSegment(sketch, "E254.MirrorCS", {"start": v(-54.23, -2.89) * mm, "end": v(-52.38, -4.58) * mm, "construction": true});
            skArc(sketch, "E255.MirrorCS", {"start": v(-6.31, -7.9) * mm, "mid": v(-6.65, -7.98) * mm, "end": v(-6.96, -7.82) * mm});
            skArc(sketch, "E256.MirrorCS", {"start": v(-47.6, -3.66) * mm, "mid": v(-48.03, -3.6) * mm, "end": v(-48.35, -3.9) * mm});
            skArc(sketch, "E257.MirrorCS", {"start": v(-64.8, 22.72) * mm, "mid": v(-64.4, 22.85) * mm, "end": v(-64.24, 23.25) * mm});
            skArc(sketch, "E258.MirrorCS", {"start": v(5.33, 8.99) * mm, "mid": v(5.68, 9.23) * mm, "end": v(6.1, 9.12) * mm});
            skArc(sketch, "E259.MirrorCS", {"start": v(-65.23, 13.17) * mm, "mid": v(-65.43, 12.88) * mm, "end": v(-65.4, 12.54) * mm});
            skLineSegment(sketch, "E260.MirrorCS", {"start": v(-64.73, 11.1) * mm, "end": v(-65.4, 12.54) * mm});
            skArc(sketch, "E261.MirrorCS", {"start": v(-36.63, -8.5) * mm, "mid": v(-37.05, -8.57) * mm, "end": v(-37.27, -8.95) * mm});
            skArc(sketch, "E262.MirrorCS", {"start": v(-58.7, 1.9) * mm, "mid": v(-58.8, 1.57) * mm, "end": v(-58.67, 1.25) * mm});
            skArc(sketch, "E263.MirrorCS", {"start": v(-6.6, -3.66) * mm, "mid": v(-6.17, -3.6) * mm, "end": v(-5.85, -3.9) * mm});
            skArc(sketch, "E264.MirrorCS", {"start": v(-47.89, -7.9) * mm, "mid": v(-47.55, -7.98) * mm, "end": v(-47.24, -7.82) * mm});
            skLineSegment(sketch, "E265.MirrorCS", {"start": v(10.52, 11.1) * mm, "end": v(11.2, 12.54) * mm});
            skLineSegment(sketch, "E266.MirrorCS", {"start": v(-62.78, 7) * mm, "end": v(-61.57, 4.93) * mm, "construction": true});
            skArc(sketch, "E267.MirrorCS", {"start": v(-41.9, -10.82) * mm, "mid": v(-41.56, -10.84) * mm, "end": v(-41.28, -10.63) * mm});
            skLineSegment(sketch, "E268.MirrorCS", {"start": v(8.58, 7) * mm, "end": v(7.37, 4.93) * mm, "construction": true});
            skArc(sketch, "E269.MirrorCS", {"start": v(10.52, 11.1) * mm, "mid": v(10.28, 10.85) * mm, "end": v(9.93, 10.82) * mm});
            skArc(sketch, "E270.MirrorCS", {"start": v(-31.42, -9.6) * mm, "mid": v(-31.81, -9.77) * mm, "end": v(-31.94, -10.18) * mm});
            skArc(sketch, "E271.MirrorCS", {"start": v(-50.02, -2.76) * mm, "mid": v(-49.82, -2.38) * mm, "end": v(-49.99, -1.98) * mm});
            skArc(sketch, "E272.MirrorCS", {"start": v(12.66, 19.67) * mm, "mid": v(12.9, 19.43) * mm, "end": v(12.93, 19.08) * mm});
            skArc(sketch, "E273.MirrorCS", {"start": v(9.42, 17.33) * mm, "mid": v(9.05, 17.54) * mm, "end": v(8.98, 17.97) * mm});
            skArc(sketch, "E274.MirrorCS", {"start": v(-33.85, -9.86) * mm, "mid": v(-33.85, -9.43) * mm, "end": v(-34.18, -9.15) * mm});
            skArc(sketch, "E275.MirrorCS", {"start": v(-66.86, 19.67) * mm, "mid": v(-67.1, 19.43) * mm, "end": v(-67.13, 19.08) * mm});
            skArc(sketch, "E276.MirrorCS", {"start": v(0.44, 1.48) * mm, "mid": v(0.2, 1.84) * mm, "end": v(0.34, 2.25) * mm});
            skArc(sketch, "E277.MirrorCS", {"start": v(-28.4, -10.3) * mm, "mid": v(-28.5, -9.88) * mm, "end": v(-28.88, -9.69) * mm});
            skArc(sketch, "E278.MirrorCS", {"start": v(-59.53, 8.99) * mm, "mid": v(-59.88, 9.23) * mm, "end": v(-60.3, 9.12) * mm});
            skArc(sketch, "E279.MirrorCS", {"start": v(-61.78, 5.3) * mm, "mid": v(-61.52, 5.08) * mm, "end": v(-61.17, 5.08) * mm});
            skLineSegment(sketch, "E280.MirrorCS", {"start": v(-65.58, 12.92) * mm, "end": v(-64.55, 10.71) * mm, "construction": true});
            skLineSegment(sketch, "E281.MirrorCS", {"start": v(11.38, 12.92) * mm, "end": v(10.34, 10.71) * mm, "construction": true});
            skLineSegment(sketch, "E282.MirrorCS", {"start": v(-47.89, -7.9) * mm, "end": v(-49.22, -7.04) * mm});
            skArc(sketch, "E283.MirrorCS", {"start": v(-0.2, -2.53) * mm, "mid": v(-0.12, -2.87) * mm, "end": v(-0.28, -3.18) * mm});
            skArc(sketch, "E284.MirrorCS", {"start": v(-54.64, 1.48) * mm, "mid": v(-54.4, 1.84) * mm, "end": v(-54.54, 2.25) * mm});
            skLineSegment(sketch, "E285.MirrorCS", {"start": v(-31.52, -13.14) * mm, "end": v(-29.02, -13.22) * mm, "construction": true});
            skArc(sketch, "E286.MirrorCS", {"start": v(-49.42, -6.42) * mm, "mid": v(-49.43, -6.77) * mm, "end": v(-49.22, -7.04) * mm});
            skArc(sketch, "E287.MirrorCS", {"start": v(-31.58, -12.72) * mm, "mid": v(-31.41, -13.02) * mm, "end": v(-31.1, -13.15) * mm});
            skLineSegment(sketch, "E288.MirrorCS", {"start": v(-58.96, 1.56) * mm, "end": v(-57.3, -0.23) * mm, "construction": true});
            skArc(sketch, "E289.MirrorCS", {"start": v(-35.6, -12.62) * mm, "mid": v(-35.25, -12.6) * mm, "end": v(-35, -12.35) * mm});
            skLineSegment(sketch, "E290.MirrorCS", {"start": v(-37.54, -12.1) * mm, "end": v(-35.18, -12.73) * mm, "construction": true});
            skLineSegment(sketch, "E291.MirrorCS", {"start": v(-49.58, -6.81) * mm, "end": v(-47.53, -8.14) * mm, "construction": true});
            skArc(sketch, "E292.MirrorCS", {"start": v(-39.78, -8.32) * mm, "mid": v(-39.72, -7.9) * mm, "end": v(-40, -7.57) * mm});
            skArc(sketch, "E293.MirrorCS", {"start": v(9.63, 20.42) * mm, "mid": v(9.9, 20.75) * mm, "end": v(10.34, 20.75) * mm});
            skArc(sketch, "E294.MirrorCS", {"start": v(4.3, 6.06) * mm, "mid": v(4, 6.37) * mm, "end": v(4.05, 6.8) * mm});
            skArc(sketch, "E295.MirrorCS", {"start": v(-42.34, -6.58) * mm, "mid": v(-42.77, -6.6) * mm, "end": v(-43.04, -6.94) * mm});
            skArc(sketch, "E296.MirrorCS", {"start": v(-2.34, -0.27) * mm, "mid": v(-1.93, -0.14) * mm, "end": v(-1.57, -0.37) * mm});
            skArc(sketch, "E297.MirrorCS", {"start": v(-63.62, 17.33) * mm, "mid": v(-63.25, 17.54) * mm, "end": v(-63.18, 17.97) * mm});
            skLineSegment(sketch, "E298.MirrorCS", {"start": v(-10.45, -10.04) * mm, "end": v(-12.69, -10.99) * mm, "construction": true});
            skLineSegment(sketch, "E299.MirrorCS", {"start": v(-67.24, 19.5) * mm, "end": v(-66.6, 17.07) * mm, "construction": true});
            skArc(sketch, "E300.MirrorCS", {"start": v(13.77, 23.55) * mm, "mid": v(13.64, 23.23) * mm, "end": v(13.33, 23.07) * mm});
            skArc(sketch, "E301.MirrorCS", {"start": v(-64.73, 11.1) * mm, "mid": v(-64.48, 10.85) * mm, "end": v(-64.13, 10.82) * mm});
            skArc(sketch, "E302.MirrorCS", {"start": v(2.06, 4.12) * mm, "mid": v(2.46, 4.28) * mm, "end": v(2.84, 4.08) * mm});
            skArc(sketch, "E303.MirrorCS", {"start": v(-66.7, 17.49) * mm, "mid": v(-66.5, 17.2) * mm, "end": v(-66.17, 17.11) * mm});
            skArc(sketch, "E304.MirrorCS", {"start": v(-62.23, 14.54) * mm, "mid": v(-62.56, 14.82) * mm, "end": v(-62.98, 14.74) * mm});
            skArc(sketch, "E305.MirrorCS", {"start": v(-4.18, -2.76) * mm, "mid": v(-4.38, -2.38) * mm, "end": v(-4.21, -1.98) * mm});
            skLineSegment(sketch, "E306.MirrorCS", {"start": v(13.04, 19.5) * mm, "end": v(12.4, 17.07) * mm, "construction": true});
            skArc(sketch, "E307.MirrorCS", {"start": v(-17.57, -8.5) * mm, "mid": v(-17.15, -8.57) * mm, "end": v(-16.93, -8.95) * mm});
            skLineSegment(sketch, "E308.MirrorCS", {"start": v(-16.66, -12.1) * mm, "end": v(-19.02, -12.73) * mm, "construction": true});
            skArc(sketch, "E309.MirrorCS", {"start": v(7.28, 11.53) * mm, "mid": v(6.96, 11.8) * mm, "end": v(6.96, 12.24) * mm});
            skArc(sketch, "E310.MirrorCS", {"start": v(-63.83, 20.42) * mm, "mid": v(-64.1, 20.75) * mm, "end": v(-64.54, 20.75) * mm});
            skLineSegment(sketch, "E311.MirrorCS", {"start": v(-57.6, 0.08) * mm, "end": v(-58.67, 1.25) * mm});
            skArc(sketch, "E312.MirrorCS", {"start": v(-57.6, 0.08) * mm, "mid": v(-57.29, -0.08) * mm, "end": v(-56.95, 0) * mm});
            skArc(sketch, "E313.MirrorCS", {"start": v(-62.46, 7.29) * mm, "mid": v(-62.63, 6.98) * mm, "end": v(-62.57, 6.64) * mm});
            skArc(sketch, "E314.MirrorCS", {"start": v(-25.8, -10.3) * mm, "mid": v(-25.7, -9.88) * mm, "end": v(-25.32, -9.69) * mm});
            skArc(sketch, "E315.MirrorCS", {"start": v(10.15, 25.78) * mm, "mid": v(10.35, 26.16) * mm, "end": v(10.77, 26.25) * mm});
            skArc(sketch, "E316.MirrorCS", {"start": v(-14.42, -8.32) * mm, "mid": v(-14.48, -7.9) * mm, "end": v(-14.2, -7.57) * mm});
            skArc(sketch, "E317.MirrorCS", {"start": v(11.03, 13.17) * mm, "mid": v(11.23, 12.88) * mm, "end": v(11.2, 12.54) * mm});
            skArc(sketch, "E318.MirrorCS", {"start": v(-52.7, -4.29) * mm, "mid": v(-52.38, -4.42) * mm, "end": v(-52.05, -4.32) * mm});
            skArc(sketch, "E319.MirrorCS", {"start": v(-10.54, -9.62) * mm, "mid": v(-10.59, -9.97) * mm, "end": v(-10.84, -10.2) * mm});
            skArc(sketch, "E320.MirrorCS", {"start": v(8.03, 14.54) * mm, "mid": v(8.36, 14.82) * mm, "end": v(8.78, 14.74) * mm});
            skArc(sketch, "E321.MirrorCS", {"start": v(-11.86, -6.58) * mm, "mid": v(-11.43, -6.6) * mm, "end": v(-11.16, -6.94) * mm});
            skArc(sketch, "E322.MirrorCS", {"start": v(-51.86, -0.27) * mm, "mid": v(-52.27, -0.14) * mm, "end": v(-52.63, -0.37) * mm});
            skArc(sketch, "E323.MirrorCS", {"start": v(-58.5, 6.06) * mm, "mid": v(-58.2, 6.37) * mm, "end": v(-58.25, 6.8) * mm});
            skArc(sketch, "E324.MirrorCS", {"start": v(8.26, 7.29) * mm, "mid": v(8.43, 6.98) * mm, "end": v(8.37, 6.64) * mm});
            skArc(sketch, "E325.MirrorCS", {"start": v(-8.82, -5.81) * mm, "mid": v(-8.96, -5.4) * mm, "end": v(-8.73, -5.04) * mm});
            skArc(sketch, "E326.MirrorCS", {"start": v(-22.78, -9.6) * mm, "mid": v(-22.39, -9.77) * mm, "end": v(-22.26, -10.18) * mm});
            skArc(sketch, "E327.MirrorCS", {"start": v(-43.66, -9.62) * mm, "mid": v(-43.61, -9.97) * mm, "end": v(-43.36, -10.2) * mm});
            skArc(sketch, "E328.MirrorCS", {"start": v(-29.44, -13.2) * mm, "mid": v(-29.11, -13.1) * mm, "end": v(-28.93, -12.8) * mm});
            skLineSegment(sketch, "E329.MirrorCS", {"start": v(-22.68, -13.14) * mm, "end": v(-25.18, -13.22) * mm, "construction": true});
            skArc(sketch, "E330.MirrorCS", {"start": v(-64.35, 25.78) * mm, "mid": v(-64.55, 26.16) * mm, "end": v(-64.97, 26.25) * mm});
            skLineSegment(sketch, "E331.MirrorCS", {"start": v(0.03, -2.89) * mm, "end": v(-1.82, -4.58) * mm, "construction": true});
            skArc(sketch, "E332.MirrorCS", {"start": v(-54, -2.53) * mm, "mid": v(-54.08, -2.87) * mm, "end": v(-53.92, -3.18) * mm});
            skArc(sketch, "E333.MirrorCS", {"start": v(-22.62, -12.72) * mm, "mid": v(-22.79, -13.02) * mm, "end": v(-23.1, -13.15) * mm});
            skLineSegment(sketch, "E334.MirrorCS", {"start": v(-4.62, -6.81) * mm, "end": v(-6.67, -8.14) * mm, "construction": true});
            skArc(sketch, "E335.MirrorCS", {"start": v(-67.97, 23.55) * mm, "mid": v(-67.84, 23.23) * mm, "end": v(-67.53, 23.07) * mm});
            skArc(sketch, "E336.MirrorCS", {"start": v(10.6, 22.72) * mm, "mid": v(10.2, 22.85) * mm, "end": v(10.04, 23.25) * mm});
            skArc(sketch, "E337.MirrorCS", {"start": v(-37.5, -11.68) * mm, "mid": v(-37.41, -12.01) * mm, "end": v(-37.13, -12.21) * mm});
            skArc(sketch, "E338.MirrorCS", {"start": v(-61.49, 11.53) * mm, "mid": v(-61.16, 11.8) * mm, "end": v(-61.16, 12.24) * mm});
            skArc(sketch, "E339.MirrorCS", {"start": v(-20.35, -9.86) * mm, "mid": v(-20.35, -9.43) * mm, "end": v(-20.02, -9.15) * mm});
            skLineSegment(sketch, "E340.MirrorCS", {"start": v(-67.97, 23.55) * mm, "end": v(-68.04, 25.13) * mm});
            skLineSegment(sketch, "E341.MirrorCS", {"start": v(13.77, 23.55) * mm, "end": v(13.84, 25.13) * mm});
            skLineSegment(sketch, "E342.MirrorCS", {"start": v(13.86, 25.56) * mm, "end": v(13.75, 23.12) * mm, "construction": true});
            skLineSegment(sketch, "E343.MirrorCS", {"start": v(-68.06, 25.56) * mm, "end": v(-67.95, 23.12) * mm, "construction": true});
            skArc(sketch, "E344.MirrorCS", {"start": v(13.45, 25.65) * mm, "mid": v(13.74, 25.47) * mm, "end": v(13.84, 25.13) * mm});
            skLineSegment(sketch, "E345.MirrorCS", {"start": v(-66.17, 17.11) * mm, "end": v(-63.62, 17.33) * mm});
            skLineSegment(sketch, "E346.MirrorCS", {"start": v(11.97, 17.11) * mm, "end": v(9.42, 17.33) * mm});
            skArc(sketch, "E347.MirrorCS", {"start": v(-67.65, 25.65) * mm, "mid": v(-67.94, 25.47) * mm, "end": v(-68.04, 25.13) * mm});
            skLineSegment(sketch, "E348.MirrorCS", {"start": v(10.77, 26.25) * mm, "end": v(13.45, 25.65) * mm});
            skLineSegment(sketch, "E349.MirrorCS", {"start": v(10.04, 23.25) * mm, "end": v(10.15, 25.78) * mm});
            skLineSegment(sketch, "E350.MirrorCS", {"start": v(6.97, 5.08) * mm, "end": v(4.3, 6.06) * mm});
            skLineSegment(sketch, "E351.MirrorCS", {"start": v(-6.96, -7.82) * mm, "end": v(-8.82, -5.81) * mm});
            skLineSegment(sketch, "E352.MirrorCS", {"start": v(-16.93, -8.95) * mm, "end": v(-16.7, -11.68) * mm});
            skLineSegment(sketch, "E353.MirrorCS", {"start": v(0.34, 2.25) * mm, "end": v(2.06, 4.12) * mm});
            skLineSegment(sketch, "E354.MirrorCS", {"start": v(-20.02, -9.15) * mm, "end": v(-17.57, -8.5) * mm});
            skLineSegment(sketch, "E355.MirrorCS", {"start": v(10.34, 20.75) * mm, "end": v(12.66, 19.67) * mm});
            skLineSegment(sketch, "E356.MirrorCS", {"start": v(13.33, 23.07) * mm, "end": v(10.6, 22.72) * mm});
            skLineSegment(sketch, "E357.MirrorCS", {"start": v(-8.73, -5.04) * mm, "end": v(-6.6, -3.66) * mm});
            skLineSegment(sketch, "E358.MirrorCS", {"start": v(-14.2, -7.57) * mm, "end": v(-11.86, -6.58) * mm});
            skLineSegment(sketch, "E359.MirrorCS", {"start": v(-2.15, -4.32) * mm, "end": v(-4.18, -2.76) * mm});
            skLineSegment(sketch, "E360.MirrorCS", {"start": v(6.1, 9.12) * mm, "end": v(8.26, 7.29) * mm});
            skLineSegment(sketch, "E361.MirrorCS", {"start": v(-22.26, -10.18) * mm, "end": v(-22.62, -12.72) * mm});
            skLineSegment(sketch, "E362.MirrorCS", {"start": v(9.93, 10.82) * mm, "end": v(7.28, 11.53) * mm});
            skLineSegment(sketch, "E363.MirrorCS", {"start": v(2.84, 4.08) * mm, "end": v(4.5, 1.9) * mm});
            skLineSegment(sketch, "E364.MirrorCS", {"start": v(-1.57, -0.37) * mm, "end": v(-0.2, -2.53) * mm});
            skLineSegment(sketch, "E365.MirrorCS", {"start": v(4.05, 6.8) * mm, "end": v(5.33, 8.99) * mm});
            skLineSegment(sketch, "E366.MirrorCS", {"start": v(-12.92, -10.63) * mm, "end": v(-14.42, -8.32) * mm});
            skLineSegment(sketch, "E367.MirrorCS", {"start": v(8.98, 17.97) * mm, "end": v(9.63, 20.42) * mm});
            skLineSegment(sketch, "E368.MirrorCS", {"start": v(-11.16, -6.94) * mm, "end": v(-10.54, -9.62) * mm});
            skLineSegment(sketch, "E369.MirrorCS", {"start": v(-5.85, -3.9) * mm, "end": v(-4.79, -6.42) * mm});
            skLineSegment(sketch, "E370.MirrorCS", {"start": v(8.78, 14.74) * mm, "end": v(11.03, 13.17) * mm});
            skLineSegment(sketch, "E371.MirrorCS", {"start": v(-25.32, -9.69) * mm, "end": v(-22.78, -9.6) * mm});
            skLineSegment(sketch, "E372.MirrorCS", {"start": v(-4.21, -1.98) * mm, "end": v(-2.34, -0.27) * mm});
            skLineSegment(sketch, "E373.MirrorCS", {"start": v(2.75, 0) * mm, "end": v(0.44, 1.48) * mm});
            skLineSegment(sketch, "E374.MirrorCS", {"start": v(6.96, 12.24) * mm, "end": v(8.03, 14.54) * mm});
            skLineSegment(sketch, "E375.MirrorCS", {"start": v(-25.27, -12.8) * mm, "end": v(-25.8, -10.3) * mm});
            skLineSegment(sketch, "E376.MirrorCS", {"start": v(-52.05, -4.32) * mm, "end": v(-50.02, -2.76) * mm});
            skPoint(sketch, "E377.MirrorP", {"position": v(-25.93, -9.7) * mm});
            skPoint(sketch, "E378.MirrorP", {"position": v(-63.99, 21) * mm});
            skPoint(sketch, "E379.MirrorP", {"position": v(-52.3, 0.14) * mm});
            skLineSegment(sketch, "E380.MirrorCS", {"start": v(-45.47, -5.04) * mm, "end": v(-47.6, -3.66) * mm});
            skPoint(sketch, "E381.MirrorP", {"position": v(5.63, 9.51) * mm});
            skLineSegment(sketch, "E382.MirrorCS", {"start": v(-64.97, 26.25) * mm, "end": v(-67.65, 25.65) * mm});
            skLineSegment(sketch, "E383.MirrorCS", {"start": v(-54.54, 2.25) * mm, "end": v(-56.26, 4.12) * mm});
            skPoint(sketch, "E384.MirrorP", {"position": v(-22.18, -9.58) * mm});
            skPoint(sketch, "E385.MirrorP", {"position": v(-16.98, -8.34) * mm});
            skPoint(sketch, "E386.MirrorP", {"position": v(-6.09, -3.34) * mm});
            skLineSegment(sketch, "E387.MirrorCS", {"start": v(-61.17, 5.08) * mm, "end": v(-58.5, 6.06) * mm});
            skPoint(sketch, "E388.MirrorP", {"position": v(-28.27, -9.7) * mm});
            skPoint(sketch, "E389.MirrorP", {"position": v(-25.18, -13.22) * mm});
            skPoint(sketch, "E390.MirrorP", {"position": v(-63.02, 17.38) * mm});
            skPoint(sketch, "E391.MirrorP", {"position": v(3.1, -0.23) * mm});
            skPoint(sketch, "E392.MirrorP", {"position": v(-20.6, -9.31) * mm});
            skPoint(sketch, "E393.MirrorP", {"position": v(-9.24, -5.37) * mm});
            skLineSegment(sketch, "E394.MirrorCS", {"start": v(-57.04, 4.08) * mm, "end": v(-58.7, 1.9) * mm});
            skLineSegment(sketch, "E395.MirrorCS", {"start": v(-48.35, -3.9) * mm, "end": v(-49.42, -6.42) * mm});
            skLineSegment(sketch, "E396.MirrorCS", {"start": v(-63.18, 17.97) * mm, "end": v(-63.83, 20.42) * mm});
            skPoint(sketch, "E397.MirrorP", {"position": v(-56.67, 4.56) * mm});
            skPoint(sketch, "E398.MirrorP", {"position": v(-41.51, -10.99) * mm});
            skPoint(sketch, "E399.MirrorP", {"position": v(10, 22.64) * mm});
            skLineSegment(sketch, "E400.MirrorCS", {"start": v(-40, -7.57) * mm, "end": v(-42.34, -6.58) * mm});
            skLineSegment(sketch, "E401.MirrorCS", {"start": v(-62.98, 14.74) * mm, "end": v(-65.23, 13.17) * mm});
            skPoint(sketch, "E402.MirrorP", {"position": v(-60.9, 11.69) * mm});
            skPoint(sketch, "E403.MirrorP", {"position": v(2.47, 4.56) * mm});
            skPoint(sketch, "E404.MirrorP", {"position": v(-54.13, 1.8) * mm});
            skPoint(sketch, "E405.MirrorP", {"position": v(-43.75, -10.04) * mm});
            skPoint(sketch, "E406.MirrorP", {"position": v(-64.2, 22.64) * mm});
            skPoint(sketch, "E407.MirrorP", {"position": v(-4.66, -2.39) * mm});
            skLineSegment(sketch, "E408.MirrorCS", {"start": v(-64.24, 23.25) * mm, "end": v(-64.35, 25.78) * mm});
            skPoint(sketch, "E409.MirrorP", {"position": v(-57.94, 6.27) * mm});
            skPoint(sketch, "E410.MirrorP", {"position": v(-10.45, -10.04) * mm});
            skPoint(sketch, "E411.MirrorP", {"position": v(7.37, 4.93) * mm});
            skPoint(sketch, "E412.MirrorP", {"position": v(-11.3, -6.35) * mm});
            skLineSegment(sketch, "E413.MirrorCS", {"start": v(-43.04, -6.94) * mm, "end": v(-43.66, -9.62) * mm});
            skPoint(sketch, "E414.MirrorP", {"position": v(-31.52, -13.14) * mm});
            skLineSegment(sketch, "E415.MirrorCS", {"start": v(-28.88, -9.69) * mm, "end": v(-31.42, -9.6) * mm});
            skPoint(sketch, "E416.MirrorP", {"position": v(6.7, 11.69) * mm});
            skLineSegment(sketch, "E417.MirrorCS", {"start": v(-49.99, -1.98) * mm, "end": v(-51.86, -0.27) * mm});
            skLineSegment(sketch, "E418.MirrorCS", {"start": v(-60.3, 9.12) * mm, "end": v(-62.46, 7.29) * mm});
            skPoint(sketch, "E419.MirrorP", {"position": v(-47.53, -8.14) * mm});
            skPoint(sketch, "E420.MirrorP", {"position": v(-6.67, -8.14) * mm});
            skPoint(sketch, "E421.MirrorP", {"position": v(-49.54, -2.39) * mm});
            skPoint(sketch, "E422.MirrorP", {"position": v(-33.6, -9.31) * mm});
            skPoint(sketch, "E423.MirrorP", {"position": v(13.04, 19.5) * mm});
            skPoint(sketch, "E424.MirrorP", {"position": v(-44.96, -5.37) * mm});
            skLineSegment(sketch, "E425.MirrorCS", {"start": v(-64.13, 10.82) * mm, "end": v(-61.49, 11.53) * mm});
            skPoint(sketch, "E426.MirrorP", {"position": v(8.58, 7) * mm});
            skLineSegment(sketch, "E427.MirrorCS", {"start": v(-37.27, -8.95) * mm, "end": v(-37.5, -11.68) * mm});
            skPoint(sketch, "E428.MirrorP", {"position": v(-22.68, -13.14) * mm});
            skPoint(sketch, "E429.MirrorP", {"position": v(-16.66, -12.1) * mm});
            skPoint(sketch, "E430.MirrorP", {"position": v(-4.62, -6.81) * mm});
            skPoint(sketch, "E431.MirrorP", {"position": v(0.03, -2.89) * mm});
            skPoint(sketch, "E432.MirrorP", {"position": v(-64.9, 17.22) * mm});
            skLineSegment(sketch, "E433.MirrorCS", {"start": v(-28.93, -12.8) * mm, "end": v(-28.4, -10.3) * mm});
            skPoint(sketch, "E434.MirrorP", {"position": v(-1.82, -4.58) * mm});
            skLineSegment(sketch, "E435.MirrorCS", {"start": v(-31.94, -10.18) * mm, "end": v(-31.58, -12.72) * mm});
            skLineSegment(sketch, "E436.MirrorCS", {"start": v(-19.2, -12.35) * mm, "end": v(-20.35, -9.86) * mm});
            skPoint(sketch, "E437.MirrorP", {"position": v(-62.78, 7) * mm});
            skPoint(sketch, "E438.MirrorP", {"position": v(-32.02, -9.58) * mm});
            skPoint(sketch, "E439.MirrorP", {"position": v(-61.57, 4.93) * mm});
            skPoint(sketch, "E440.MirrorP", {"position": v(-67.24, 19.5) * mm});
            skPoint(sketch, "E441.MirrorP", {"position": v(-64.55, 10.71) * mm});
            skPoint(sketch, "E442.MirrorP", {"position": v(-59.83, 9.51) * mm});
            skPoint(sketch, "E443.MirrorP", {"position": v(-1.9, 0.14) * mm});
            skPoint(sketch, "E444.MirrorP", {"position": v(12.4, 17.07) * mm});
            skPoint(sketch, "E445.MirrorP", {"position": v(8.82, 17.38) * mm});
            skPoint(sketch, "E446.MirrorP", {"position": v(-0.07, 1.8) * mm});
            skPoint(sketch, "E447.MirrorP", {"position": v(-49.58, -6.81) * mm});
            skPoint(sketch, "E448.MirrorP", {"position": v(-42.9, -6.35) * mm});
            skLineSegment(sketch, "E449.MirrorCS", {"start": v(-61.16, 12.24) * mm, "end": v(-62.23, 14.54) * mm});
            skLineSegment(sketch, "E450.MirrorCS", {"start": v(-41.28, -10.63) * mm, "end": v(-39.78, -8.32) * mm});
            skPoint(sketch, "E451.MirrorP", {"position": v(-35.18, -12.73) * mm});
            skPoint(sketch, "E452.MirrorP", {"position": v(11.38, 12.92) * mm});
            skPoint(sketch, "E453.MirrorP", {"position": v(-48.12, -3.34) * mm});
            skPoint(sketch, "E454.MirrorP", {"position": v(4.76, 1.56) * mm});
            skLineSegment(sketch, "E455.MirrorCS", {"start": v(-58.25, 6.8) * mm, "end": v(-59.53, 8.99) * mm});
            skPoint(sketch, "E456.MirrorP", {"position": v(-39.45, -7.8) * mm});
            skPoint(sketch, "E457.MirrorP", {"position": v(9.79, 21) * mm});
            skPoint(sketch, "E458.MirrorP", {"position": v(-66.6, 17.07) * mm});
            skPoint(sketch, "E459.MirrorP", {"position": v(-12.69, -10.99) * mm});
            skPoint(sketch, "E460.MirrorP", {"position": v(-54.23, -2.89) * mm});
            skPoint(sketch, "E461.MirrorP", {"position": v(-19.02, -12.73) * mm});
            skLineSegment(sketch, "E462.MirrorCS", {"start": v(-64.54, 20.75) * mm, "end": v(-66.86, 19.67) * mm});
            skPoint(sketch, "E463.MirrorP", {"position": v(-37.22, -8.34) * mm});
            skLineSegment(sketch, "E464.MirrorCS", {"start": v(-34.18, -9.15) * mm, "end": v(-36.63, -8.5) * mm});
            skPoint(sketch, "E465.MirrorP", {"position": v(-58.96, 1.56) * mm});
            skPoint(sketch, "E466.MirrorP", {"position": v(-29.02, -13.22) * mm});
            skPoint(sketch, "E467.MirrorP", {"position": v(-14.75, -7.8) * mm});
            skPoint(sketch, "E468.MirrorP", {"position": v(-52.38, -4.58) * mm});
            skLineSegment(sketch, "E469.MirrorCS", {"start": v(-52.63, -0.37) * mm, "end": v(-54, -2.53) * mm});
            skPoint(sketch, "E470.MirrorP", {"position": v(8.29, 15.09) * mm});
            skLineSegment(sketch, "E471.MirrorCS", {"start": v(-47.24, -7.82) * mm, "end": v(-45.38, -5.81) * mm});
            skPoint(sketch, "E472.MirrorP", {"position": v(-37.54, -12.1) * mm});
            skPoint(sketch, "E473.MirrorP", {"position": v(-65.58, 12.92) * mm});
            skPoint(sketch, "E474.MirrorP", {"position": v(10.7, 17.22) * mm});
            skLineSegment(sketch, "E475.MirrorCS", {"start": v(-56.95, 0) * mm, "end": v(-54.64, 1.48) * mm});
            skPoint(sketch, "E476.MirrorP", {"position": v(10.34, 10.71) * mm});
            skLineSegment(sketch, "E477.MirrorCS", {"start": v(-35, -12.35) * mm, "end": v(-33.85, -9.86) * mm});
            skPoint(sketch, "E478.MirrorP", {"position": v(3.74, 6.27) * mm});
            skLineSegment(sketch, "E479.MirrorCS", {"start": v(-67.53, 23.07) * mm, "end": v(-64.8, 22.72) * mm});
            skPoint(sketch, "E480.MirrorP", {"position": v(-62.49, 15.09) * mm});
            skPoint(sketch, "E481.MirrorP", {"position": v(-57.3, -0.23) * mm});
            skPoint(sketch, "E482.MirrorP", {"position": v(-68.06, 25.56) * mm});
            skPoint(sketch, "E483.MirrorP", {"position": v(13.86, 25.56) * mm});
            skPoint(sketch, "E484.MirrorP", {"position": v(13.75, 23.12) * mm});
            skPoint(sketch, "E485.MirrorP", {"position": v(-67.95, 23.12) * mm});
            skSolve(sketch);
        }
        {
            var Q0;
            Q0=qCreatedBy(makeId("Front.planeOp"),FACE);
            var sketch = newSketch(context, id + "F1", { "sketchPlane" : qUnion([Q0])});
            skCircle(sketch, "E486", {"center": v(23.04, -32.45) * mm, "radius": 19.05 * mm});
            skCircle(sketch, "E487", {"center": v(23.04, -32.45) * mm, "radius": 6.35 * mm});
            skLineSegment(sketch, "E488", {"start": v(23.04, -13.4) * mm, "end": v(23.04, -51.5) * mm, "construction": true});
            skLineSegment(sketch, "E489", {"start": v(4, -32.45) * mm, "end": v(42.1, -32.45) * mm, "construction": true});
            skLineSegment(sketch, "E490", {"start": v(41.13, -28.9) * mm, "end": v(41.3, -30.83) * mm});
            skLineSegment(sketch, "E491", {"start": v(44.41, -28.59) * mm, "end": v(41.68, -28.35) * mm});
            skLineSegment(sketch, "E492", {"start": v(41.94, -31.28) * mm, "end": v(44.59, -30.57) * mm});
            skLineSegment(sketch, "E493", {"start": v(44.88, -29.05) * mm, "end": v(44.96, -30.03) * mm});
            skPoint(sketch, "E494.visualSharp", {"position": v(44.84, -28.63) * mm});
            skArc(sketch, "E494.filletArc", {"start": v(44.88, -29.05) * mm, "mid": v(44.73, -28.74) * mm, "end": v(44.41, -28.59) * mm});
            skPoint(sketch, "E495.visualSharp", {"position": v(41.08, -28.3) * mm});
            skArc(sketch, "E495.filletArc", {"start": v(41.68, -28.35) * mm, "mid": v(41.28, -28.5) * mm, "end": v(41.13, -28.9) * mm});
            skPoint(sketch, "E496.visualSharp", {"position": v(41.35, -31.43) * mm});
            skArc(sketch, "E496.filletArc", {"start": v(41.3, -30.83) * mm, "mid": v(41.52, -31.2) * mm, "end": v(41.94, -31.28) * mm});
            skPoint(sketch, "E497.visualSharp", {"position": v(45, -30.46) * mm});
            skArc(sketch, "E497.filletArc", {"start": v(44.59, -30.57) * mm, "mid": v(44.87, -30.37) * mm, "end": v(44.96, -30.03) * mm});
            skLineSegment(sketch, "E498.0", {"start": v(45, -30.46) * mm, "end": v(44.84, -28.63) * mm, "construction": true});
            skLineSegment(sketch, "E499", {"start": v(38.78, -23.42) * mm, "end": v(39.73, -25.1) * mm});
            skLineSegment(sketch, "E500", {"start": v(41.64, -21.78) * mm, "end": v(39.05, -22.69) * mm});
            skLineSegment(sketch, "E501", {"start": v(40.5, -25.25) * mm, "end": v(42.61, -23.51) * mm});
            skLineSegment(sketch, "E502", {"start": v(42.25, -22.01) * mm, "end": v(42.73, -22.87) * mm});
            skPoint(sketch, "E503.visualSharp", {"position": v(42.04, -21.64) * mm});
            skArc(sketch, "E503.filletArc", {"start": v(42.25, -22.01) * mm, "mid": v(41.99, -21.78) * mm, "end": v(41.64, -21.78) * mm});
            skPoint(sketch, "E504.visualSharp", {"position": v(38.48, -22.89) * mm});
            skArc(sketch, "E504.filletArc", {"start": v(39.05, -22.69) * mm, "mid": v(38.75, -22.99) * mm, "end": v(38.78, -23.42) * mm});
            skPoint(sketch, "E505.visualSharp", {"position": v(40.02, -25.63) * mm});
            skArc(sketch, "E505.filletArc", {"start": v(39.73, -25.1) * mm, "mid": v(40.08, -25.36) * mm, "end": v(40.5, -25.25) * mm});
            skPoint(sketch, "E506.visualSharp", {"position": v(42.94, -23.24) * mm});
            skArc(sketch, "E506.filletArc", {"start": v(42.61, -23.51) * mm, "mid": v(42.8, -23.21) * mm, "end": v(42.73, -22.87) * mm});
            skLineSegment(sketch, "E507.0", {"start": v(42.94, -23.24) * mm, "end": v(42.04, -21.64) * mm, "construction": true});
            skLineSegment(sketch, "E508", {"start": v(35.02, -18.63) * mm, "end": v(36.4, -20) * mm});
            skLineSegment(sketch, "E509", {"start": v(37.34, -16.28) * mm, "end": v(35.1, -17.86) * mm});
            skLineSegment(sketch, "E510", {"start": v(37.17, -19.94) * mm, "end": v(38.74, -17.69) * mm});
            skLineSegment(sketch, "E511", {"start": v(37.99, -16.34) * mm, "end": v(38.69, -17.04) * mm});
            skPoint(sketch, "E512.visualSharp", {"position": v(37.69, -16.04) * mm});
            skArc(sketch, "E512.filletArc", {"start": v(37.99, -16.34) * mm, "mid": v(37.67, -16.2) * mm, "end": v(37.34, -16.28) * mm});
            skPoint(sketch, "E513.visualSharp", {"position": v(34.6, -18.2) * mm});
            skArc(sketch, "E513.filletArc", {"start": v(35.1, -17.86) * mm, "mid": v(34.88, -18.23) * mm, "end": v(35.02, -18.63) * mm});
            skPoint(sketch, "E514.visualSharp", {"position": v(36.82, -20.43) * mm});
            skArc(sketch, "E514.filletArc", {"start": v(36.4, -20) * mm, "mid": v(36.8, -20.15) * mm, "end": v(37.17, -19.94) * mm});
            skPoint(sketch, "E515.visualSharp", {"position": v(38.99, -17.34) * mm});
            skArc(sketch, "E515.filletArc", {"start": v(38.74, -17.69) * mm, "mid": v(38.83, -17.35) * mm, "end": v(38.69, -17.04) * mm});
            skLineSegment(sketch, "E516.0", {"start": v(38.99, -17.34) * mm, "end": v(37.69, -16.04) * mm, "construction": true});
            skLineSegment(sketch, "E517", {"start": v(30.44, -15.62) * mm, "end": v(32.12, -16.6) * mm});
            skLineSegment(sketch, "E518", {"start": v(32.07, -12.76) * mm, "end": v(30.3, -14.86) * mm});
            skLineSegment(sketch, "E519", {"start": v(32.85, -16.33) * mm, "end": v(33.79, -13.75) * mm});
            skLineSegment(sketch, "E520", {"start": v(32.71, -12.64) * mm, "end": v(33.57, -13.14) * mm});
            skPoint(sketch, "E521.visualSharp", {"position": v(32.34, -12.43) * mm});
            skArc(sketch, "E521.filletArc", {"start": v(32.71, -12.64) * mm, "mid": v(32.37, -12.58) * mm, "end": v(32.07, -12.76) * mm});
            skPoint(sketch, "E522.visualSharp", {"position": v(29.92, -15.32) * mm});
            skArc(sketch, "E522.filletArc", {"start": v(30.3, -14.86) * mm, "mid": v(30.2, -15.27) * mm, "end": v(30.44, -15.62) * mm});
            skPoint(sketch, "E523.visualSharp", {"position": v(32.65, -16.9) * mm});
            skArc(sketch, "E523.filletArc", {"start": v(32.12, -16.6) * mm, "mid": v(32.55, -16.63) * mm, "end": v(32.85, -16.33) * mm});
            skPoint(sketch, "E524.visualSharp", {"position": v(33.94, -13.35) * mm});
            skArc(sketch, "E524.filletArc", {"start": v(33.79, -13.75) * mm, "mid": v(33.79, -13.4) * mm, "end": v(33.57, -13.14) * mm});
            skLineSegment(sketch, "E525.0", {"start": v(33.94, -13.35) * mm, "end": v(32.34, -12.43) * mm, "construction": true});
            skLineSegment(sketch, "E526", {"start": v(24.93, -14.08) * mm, "end": v(26.84, -14.42) * mm});
            skLineSegment(sketch, "E527", {"start": v(25.47, -10.83) * mm, "end": v(24.54, -13.41) * mm});
            skLineSegment(sketch, "E528", {"start": v(27.43, -13.92) * mm, "end": v(27.43, -11.18) * mm});
            skLineSegment(sketch, "E529", {"start": v(26.04, -10.5) * mm, "end": v(27.01, -10.68) * mm});
            skPoint(sketch, "E530.visualSharp", {"position": v(25.62, -10.43) * mm});
            skArc(sketch, "E530.filletArc", {"start": v(26.04, -10.5) * mm, "mid": v(25.7, -10.57) * mm, "end": v(25.47, -10.83) * mm});
            skPoint(sketch, "E531.visualSharp", {"position": v(24.33, -13.98) * mm});
            skArc(sketch, "E531.filletArc", {"start": v(24.54, -13.41) * mm, "mid": v(24.57, -13.84) * mm, "end": v(24.93, -14.08) * mm});
            skPoint(sketch, "E532.visualSharp", {"position": v(27.43, -14.53) * mm});
            skArc(sketch, "E532.filletArc", {"start": v(26.84, -14.42) * mm, "mid": v(27.25, -14.31) * mm, "end": v(27.43, -13.92) * mm});
            skPoint(sketch, "E533.visualSharp", {"position": v(27.43, -10.75) * mm});
            skArc(sketch, "E533.filletArc", {"start": v(27.43, -11.18) * mm, "mid": v(27.31, -10.85) * mm, "end": v(27.01, -10.68) * mm});
            skLineSegment(sketch, "E534.0", {"start": v(27.43, -10.75) * mm, "end": v(25.62, -10.43) * mm, "construction": true});
            skLineSegment(sketch, "E535.MirrorCS", {"start": v(20.05, -10.5) * mm, "end": v(19.08, -10.68) * mm});
            skArc(sketch, "E536.MirrorCS", {"start": v(20.05, -10.5) * mm, "mid": v(20.4, -10.57) * mm, "end": v(20.61, -10.83) * mm});
            skLineSegment(sketch, "E537.MirrorCS", {"start": v(1.09, -30.46) * mm, "end": v(1.25, -28.63) * mm, "construction": true});
            skArc(sketch, "E538.MirrorCS", {"start": v(18.66, -11.18) * mm, "mid": v(18.78, -10.85) * mm, "end": v(19.08, -10.68) * mm});
            skLineSegment(sketch, "E539.MirrorCS", {"start": v(1.21, -29.05) * mm, "end": v(1.13, -30.03) * mm});
            skArc(sketch, "E540.MirrorCS", {"start": v(13.38, -12.64) * mm, "mid": v(13.72, -12.58) * mm, "end": v(14.02, -12.76) * mm});
            skArc(sketch, "E541.MirrorCS", {"start": v(11, -17.86) * mm, "mid": v(11.21, -18.23) * mm, "end": v(11.06, -18.63) * mm});
            skArc(sketch, "E542.MirrorCS", {"start": v(6.36, -25.1) * mm, "mid": v(6.01, -25.36) * mm, "end": v(5.6, -25.25) * mm});
            skArc(sketch, "E543.MirrorCS", {"start": v(8.1, -16.34) * mm, "mid": v(8.41, -16.2) * mm, "end": v(8.75, -16.28) * mm});
            skLineSegment(sketch, "E544.MirrorCS", {"start": v(13.38, -12.64) * mm, "end": v(12.52, -13.14) * mm});
            skArc(sketch, "E545.MirrorCS", {"start": v(7.35, -17.69) * mm, "mid": v(7.26, -17.35) * mm, "end": v(7.4, -17.04) * mm});
            skArc(sketch, "E546.MirrorCS", {"start": v(3.48, -23.51) * mm, "mid": v(3.3, -23.21) * mm, "end": v(3.35, -22.87) * mm});
            skArc(sketch, "E547.MirrorCS", {"start": v(13.97, -16.6) * mm, "mid": v(13.54, -16.63) * mm, "end": v(13.24, -16.33) * mm});
            skArc(sketch, "E548.MirrorCS", {"start": v(15.78, -14.86) * mm, "mid": v(15.9, -15.27) * mm, "end": v(15.65, -15.62) * mm});
            skArc(sketch, "E549.MirrorCS", {"start": v(9.7, -20) * mm, "mid": v(9.29, -20.15) * mm, "end": v(8.92, -19.94) * mm});
            skArc(sketch, "E550.MirrorCS", {"start": v(7.04, -22.69) * mm, "mid": v(7.34, -22.99) * mm, "end": v(7.31, -23.42) * mm});
            skLineSegment(sketch, "E551.MirrorCS", {"start": v(8.1, -16.34) * mm, "end": v(7.4, -17.04) * mm});
            skArc(sketch, "E552.MirrorCS", {"start": v(1.5, -30.57) * mm, "mid": v(1.22, -30.37) * mm, "end": v(1.13, -30.03) * mm});
            skLineSegment(sketch, "E553.MirrorCS", {"start": v(7.1, -17.34) * mm, "end": v(8.4, -16.04) * mm, "construction": true});
            skLineSegment(sketch, "E554.MirrorCS", {"start": v(18.66, -10.75) * mm, "end": v(20.47, -10.43) * mm, "construction": true});
            skArc(sketch, "E555.MirrorCS", {"start": v(3.84, -22.01) * mm, "mid": v(4.1, -21.78) * mm, "end": v(4.45, -21.78) * mm});
            skArc(sketch, "E556.MirrorCS", {"start": v(12.3, -13.75) * mm, "mid": v(12.3, -13.4) * mm, "end": v(12.52, -13.14) * mm});
            skArc(sketch, "E557.MirrorCS", {"start": v(21.55, -13.41) * mm, "mid": v(21.51, -13.84) * mm, "end": v(21.16, -14.08) * mm});
            skLineSegment(sketch, "E558.MirrorCS", {"start": v(3.84, -22.01) * mm, "end": v(3.35, -22.87) * mm});
            skArc(sketch, "E559.MirrorCS", {"start": v(4.79, -30.83) * mm, "mid": v(4.57, -31.2) * mm, "end": v(4.15, -31.28) * mm});
            skLineSegment(sketch, "E560.MirrorCS", {"start": v(3.15, -23.24) * mm, "end": v(4.05, -21.64) * mm, "construction": true});
            skLineSegment(sketch, "E561.MirrorCS", {"start": v(12.15, -13.35) * mm, "end": v(13.75, -12.43) * mm, "construction": true});
            skArc(sketch, "E562.MirrorCS", {"start": v(19.25, -14.42) * mm, "mid": v(18.84, -14.31) * mm, "end": v(18.66, -13.92) * mm});
            skArc(sketch, "E563.MirrorCS", {"start": v(1.21, -29.05) * mm, "mid": v(1.36, -28.74) * mm, "end": v(1.67, -28.59) * mm});
            skArc(sketch, "E564.MirrorCS", {"start": v(4.4, -28.35) * mm, "mid": v(4.8, -28.5) * mm, "end": v(4.96, -28.9) * mm});
            skPoint(sketch, "E565.MirrorP", {"position": v(4.73, -31.43) * mm});
            skPoint(sketch, "E566.MirrorP", {"position": v(9.27, -20.43) * mm});
            skPoint(sketch, "E567.MirrorP", {"position": v(13.44, -16.9) * mm});
            skPoint(sketch, "E568.MirrorP", {"position": v(21.76, -13.98) * mm});
            skPoint(sketch, "E569.MirrorP", {"position": v(7.6, -22.89) * mm});
            skPoint(sketch, "E570.MirrorP", {"position": v(3.15, -23.24) * mm});
            skPoint(sketch, "E571.MirrorP", {"position": v(18.66, -10.75) * mm});
            skLineSegment(sketch, "E572.MirrorCS", {"start": v(15.65, -15.62) * mm, "end": v(13.97, -16.6) * mm});
            skLineSegment(sketch, "E573.MirrorCS", {"start": v(18.66, -13.92) * mm, "end": v(18.66, -11.18) * mm});
            skLineSegment(sketch, "E574.MirrorCS", {"start": v(13.24, -16.33) * mm, "end": v(12.3, -13.75) * mm});
            skLineSegment(sketch, "E575.MirrorCS", {"start": v(8.75, -16.28) * mm, "end": v(11, -17.86) * mm});
            skLineSegment(sketch, "E576.MirrorCS", {"start": v(14.02, -12.76) * mm, "end": v(15.78, -14.86) * mm});
            skLineSegment(sketch, "E577.MirrorCS", {"start": v(5.6, -25.25) * mm, "end": v(3.48, -23.51) * mm});
            skLineSegment(sketch, "E578.MirrorCS", {"start": v(8.92, -19.94) * mm, "end": v(7.35, -17.69) * mm});
            skPoint(sketch, "E579.MirrorP", {"position": v(1.09, -30.46) * mm});
            skPoint(sketch, "E580.MirrorP", {"position": v(7.1, -17.34) * mm});
            skLineSegment(sketch, "E581.MirrorCS", {"start": v(4.45, -21.78) * mm, "end": v(7.04, -22.69) * mm});
            skPoint(sketch, "E582.MirrorP", {"position": v(12.15, -13.35) * mm});
            skPoint(sketch, "E583.MirrorP", {"position": v(20.47, -10.43) * mm});
            skLineSegment(sketch, "E584.MirrorCS", {"start": v(7.31, -23.42) * mm, "end": v(6.36, -25.1) * mm});
            skLineSegment(sketch, "E585.MirrorCS", {"start": v(1.67, -28.59) * mm, "end": v(4.4, -28.35) * mm});
            skLineSegment(sketch, "E586.MirrorCS", {"start": v(4.96, -28.9) * mm, "end": v(4.79, -30.83) * mm});
            skLineSegment(sketch, "E587.MirrorCS", {"start": v(4.15, -31.28) * mm, "end": v(1.5, -30.57) * mm});
            skPoint(sketch, "E588.MirrorP", {"position": v(18.66, -14.53) * mm});
            skPoint(sketch, "E589.MirrorP", {"position": v(4.05, -21.64) * mm});
            skLineSegment(sketch, "E590.MirrorCS", {"start": v(11.06, -18.63) * mm, "end": v(9.7, -20) * mm});
            skPoint(sketch, "E591.MirrorP", {"position": v(6.06, -25.63) * mm});
            skPoint(sketch, "E592.MirrorP", {"position": v(13.75, -12.43) * mm});
            skLineSegment(sketch, "E593.MirrorCS", {"start": v(21.16, -14.08) * mm, "end": v(19.25, -14.42) * mm});
            skLineSegment(sketch, "E594.MirrorCS", {"start": v(20.61, -10.83) * mm, "end": v(21.55, -13.41) * mm});
            skPoint(sketch, "E595.MirrorP", {"position": v(5, -28.3) * mm});
            skPoint(sketch, "E596.MirrorP", {"position": v(11.5, -18.2) * mm});
            skPoint(sketch, "E597.MirrorP", {"position": v(16.17, -15.32) * mm});
            skPoint(sketch, "E598.MirrorP", {"position": v(1.25, -28.63) * mm});
            skPoint(sketch, "E599.MirrorP", {"position": v(8.4, -16.04) * mm});
            skLineSegment(sketch, "E600.MirrorCS", {"start": v(42.25, -42.88) * mm, "end": v(42.73, -42.02) * mm});
            skArc(sketch, "E601.MirrorCS", {"start": v(37.99, -48.55) * mm, "mid": v(37.67, -48.7) * mm, "end": v(37.34, -48.6) * mm});
            skLineSegment(sketch, "E602.MirrorCS", {"start": v(32.71, -52.25) * mm, "end": v(33.57, -51.76) * mm});
            skArc(sketch, "E603.MirrorCS", {"start": v(20.05, -54.39) * mm, "mid": v(20.4, -54.32) * mm, "end": v(20.61, -54.06) * mm});
            skArc(sketch, "E604.MirrorCS", {"start": v(1.5, -34.32) * mm, "mid": v(1.22, -34.52) * mm, "end": v(1.13, -34.86) * mm});
            skLineSegment(sketch, "E605.MirrorCS", {"start": v(37.99, -48.55) * mm, "end": v(38.69, -47.85) * mm});
            skLineSegment(sketch, "E606.MirrorCS", {"start": v(8.1, -48.55) * mm, "end": v(7.4, -47.85) * mm});
            skArc(sketch, "E607.MirrorCS", {"start": v(44.59, -34.32) * mm, "mid": v(44.87, -34.52) * mm, "end": v(44.96, -34.86) * mm});
            skArc(sketch, "E608.MirrorCS", {"start": v(41.3, -34.06) * mm, "mid": v(41.52, -33.69) * mm, "end": v(41.94, -33.61) * mm});
            skArc(sketch, "E609.MirrorCS", {"start": v(41.68, -36.54) * mm, "mid": v(41.28, -36.4) * mm, "end": v(41.13, -36) * mm});
            skArc(sketch, "E610.MirrorCS", {"start": v(44.88, -35.84) * mm, "mid": v(44.73, -36.16) * mm, "end": v(44.41, -36.3) * mm});
            skLineSegment(sketch, "E611.MirrorCS", {"start": v(44.88, -35.84) * mm, "end": v(44.96, -34.86) * mm});
            skArc(sketch, "E612.MirrorCS", {"start": v(7.04, -42.2) * mm, "mid": v(7.34, -41.9) * mm, "end": v(7.31, -41.48) * mm});
            skArc(sketch, "E613.MirrorCS", {"start": v(27.43, -53.71) * mm, "mid": v(27.31, -54.04) * mm, "end": v(27.01, -54.21) * mm});
            skArc(sketch, "E614.MirrorCS", {"start": v(9.7, -44.89) * mm, "mid": v(9.29, -44.74) * mm, "end": v(8.92, -44.96) * mm});
            skArc(sketch, "E615.MirrorCS", {"start": v(26.84, -50.47) * mm, "mid": v(27.25, -50.58) * mm, "end": v(27.43, -50.97) * mm});
            skArc(sketch, "E616.MirrorCS", {"start": v(15.78, -50.03) * mm, "mid": v(15.9, -49.62) * mm, "end": v(15.65, -49.27) * mm});
            skArc(sketch, "E617.MirrorCS", {"start": v(4.4, -36.54) * mm, "mid": v(4.8, -36.4) * mm, "end": v(4.96, -36) * mm});
            skArc(sketch, "E618.MirrorCS", {"start": v(24.54, -51.48) * mm, "mid": v(24.57, -51.05) * mm, "end": v(24.93, -50.8) * mm});
            skArc(sketch, "E619.MirrorCS", {"start": v(13.97, -48.3) * mm, "mid": v(13.54, -48.26) * mm, "end": v(13.24, -48.57) * mm});
            skArc(sketch, "E620.MirrorCS", {"start": v(1.21, -35.84) * mm, "mid": v(1.36, -36.16) * mm, "end": v(1.67, -36.3) * mm});
            skLineSegment(sketch, "E621.MirrorCS", {"start": v(42.94, -41.65) * mm, "end": v(42.04, -43.25) * mm, "construction": true});
            skLineSegment(sketch, "E622.MirrorCS", {"start": v(7.1, -47.55) * mm, "end": v(8.4, -48.85) * mm, "construction": true});
            skArc(sketch, "E623.MirrorCS", {"start": v(32.71, -52.25) * mm, "mid": v(32.37, -52.3) * mm, "end": v(32.07, -52.13) * mm});
            skArc(sketch, "E624.MirrorCS", {"start": v(35.1, -47.04) * mm, "mid": v(34.88, -46.66) * mm, "end": v(35.02, -46.26) * mm});
            skArc(sketch, "E625.MirrorCS", {"start": v(38.74, -47.2) * mm, "mid": v(38.83, -47.54) * mm, "end": v(38.69, -47.85) * mm});
            skArc(sketch, "E626.MirrorCS", {"start": v(3.84, -42.88) * mm, "mid": v(4.1, -43.1) * mm, "end": v(4.45, -43.11) * mm});
            skArc(sketch, "E627.MirrorCS", {"start": v(32.12, -48.3) * mm, "mid": v(32.55, -48.26) * mm, "end": v(32.85, -48.57) * mm});
            skArc(sketch, "E628.MirrorCS", {"start": v(42.25, -42.88) * mm, "mid": v(41.99, -43.1) * mm, "end": v(41.64, -43.11) * mm});
            skArc(sketch, "E629.MirrorCS", {"start": v(8.1, -48.55) * mm, "mid": v(8.41, -48.7) * mm, "end": v(8.75, -48.6) * mm});
            skArc(sketch, "E630.MirrorCS", {"start": v(26.04, -54.39) * mm, "mid": v(25.7, -54.32) * mm, "end": v(25.47, -54.06) * mm});
            skArc(sketch, "E631.MirrorCS", {"start": v(3.48, -41.38) * mm, "mid": v(3.3, -41.68) * mm, "end": v(3.35, -42.02) * mm});
            skArc(sketch, "E632.MirrorCS", {"start": v(42.61, -41.38) * mm, "mid": v(42.8, -41.68) * mm, "end": v(42.73, -42.02) * mm});
            skArc(sketch, "E633.MirrorCS", {"start": v(4.79, -34.06) * mm, "mid": v(4.57, -33.69) * mm, "end": v(4.15, -33.61) * mm});
            skArc(sketch, "E634.MirrorCS", {"start": v(39.05, -42.2) * mm, "mid": v(38.75, -41.9) * mm, "end": v(38.78, -41.48) * mm});
            skArc(sketch, "E635.MirrorCS", {"start": v(39.73, -39.79) * mm, "mid": v(40.08, -39.54) * mm, "end": v(40.5, -39.64) * mm});
            skLineSegment(sketch, "E636.MirrorCS", {"start": v(12.15, -51.54) * mm, "end": v(13.75, -52.46) * mm, "construction": true});
            skArc(sketch, "E637.MirrorCS", {"start": v(7.35, -47.2) * mm, "mid": v(7.26, -47.54) * mm, "end": v(7.4, -47.85) * mm});
            skLineSegment(sketch, "E638.MirrorCS", {"start": v(3.15, -41.65) * mm, "end": v(4.05, -43.25) * mm, "construction": true});
            skLineSegment(sketch, "E639.MirrorCS", {"start": v(13.38, -52.25) * mm, "end": v(12.52, -51.76) * mm});
            skArc(sketch, "E640.MirrorCS", {"start": v(13.38, -52.25) * mm, "mid": v(13.72, -52.3) * mm, "end": v(14.02, -52.13) * mm});
            skArc(sketch, "E641.MirrorCS", {"start": v(12.3, -51.14) * mm, "mid": v(12.3, -51.49) * mm, "end": v(12.52, -51.76) * mm});
            skArc(sketch, "E642.MirrorCS", {"start": v(6.36, -39.79) * mm, "mid": v(6.01, -39.54) * mm, "end": v(5.6, -39.64) * mm});
            skArc(sketch, "E643.MirrorCS", {"start": v(33.79, -51.14) * mm, "mid": v(33.79, -51.49) * mm, "end": v(33.57, -51.76) * mm});
            skArc(sketch, "E644.MirrorCS", {"start": v(18.66, -53.71) * mm, "mid": v(18.78, -54.04) * mm, "end": v(19.08, -54.21) * mm});
            skArc(sketch, "E645.MirrorCS", {"start": v(21.55, -51.48) * mm, "mid": v(21.51, -51.05) * mm, "end": v(21.16, -50.8) * mm});
            skLineSegment(sketch, "E646.MirrorCS", {"start": v(26.04, -54.39) * mm, "end": v(27.01, -54.21) * mm});
            skArc(sketch, "E647.MirrorCS", {"start": v(36.4, -44.89) * mm, "mid": v(36.8, -44.74) * mm, "end": v(37.17, -44.96) * mm});
            skLineSegment(sketch, "E648.MirrorCS", {"start": v(3.84, -42.88) * mm, "end": v(3.35, -42.02) * mm});
            skArc(sketch, "E649.MirrorCS", {"start": v(30.3, -50.03) * mm, "mid": v(30.2, -49.62) * mm, "end": v(30.44, -49.27) * mm});
            skLineSegment(sketch, "E650.MirrorCS", {"start": v(38.99, -47.55) * mm, "end": v(37.69, -48.85) * mm, "construction": true});
            skArc(sketch, "E651.MirrorCS", {"start": v(11, -47.04) * mm, "mid": v(11.21, -46.66) * mm, "end": v(11.06, -46.26) * mm});
            skLineSegment(sketch, "E652.MirrorCS", {"start": v(33.94, -51.54) * mm, "end": v(32.34, -52.46) * mm, "construction": true});
            skLineSegment(sketch, "E653.MirrorCS", {"start": v(45, -34.43) * mm, "end": v(44.84, -36.27) * mm, "construction": true});
            skLineSegment(sketch, "E654.MirrorCS", {"start": v(20.05, -54.39) * mm, "end": v(19.08, -54.21) * mm});
            skLineSegment(sketch, "E655.MirrorCS", {"start": v(27.43, -54.14) * mm, "end": v(25.62, -54.46) * mm, "construction": true});
            skLineSegment(sketch, "E656.MirrorCS", {"start": v(1.21, -35.84) * mm, "end": v(1.13, -34.86) * mm});
            skArc(sketch, "E657.MirrorCS", {"start": v(19.25, -50.47) * mm, "mid": v(18.84, -50.58) * mm, "end": v(18.66, -50.97) * mm});
            skPoint(sketch, "E658.MirrorP", {"position": v(44.84, -36.27) * mm});
            skPoint(sketch, "E659.MirrorP", {"position": v(37.69, -48.85) * mm});
            skPoint(sketch, "E660.MirrorP", {"position": v(32.34, -52.46) * mm});
            skLineSegment(sketch, "E661.MirrorCS", {"start": v(8.75, -48.6) * mm, "end": v(11, -47.04) * mm});
            skPoint(sketch, "E662.MirrorP", {"position": v(4.05, -43.25) * mm});
            skLineSegment(sketch, "E663.MirrorCS", {"start": v(13.24, -48.57) * mm, "end": v(12.3, -51.14) * mm});
            skLineSegment(sketch, "E664.MirrorCS", {"start": v(32.85, -48.57) * mm, "end": v(33.79, -51.14) * mm});
            skPoint(sketch, "E665.MirrorP", {"position": v(18.66, -50.37) * mm});
            skLineSegment(sketch, "E666.MirrorCS", {"start": v(41.94, -33.61) * mm, "end": v(44.59, -34.32) * mm});
            skLineSegment(sketch, "E667.MirrorCS", {"start": v(44.41, -36.3) * mm, "end": v(41.68, -36.54) * mm});
            skLineSegment(sketch, "E668.MirrorCS", {"start": v(41.13, -36) * mm, "end": v(41.3, -34.06) * mm});
            skLineSegment(sketch, "E669.MirrorCS", {"start": v(40.5, -39.64) * mm, "end": v(42.61, -41.38) * mm});
            skLineSegment(sketch, "E670.MirrorCS", {"start": v(41.64, -43.11) * mm, "end": v(39.05, -42.2) * mm});
            skLineSegment(sketch, "E671.MirrorCS", {"start": v(38.78, -41.48) * mm, "end": v(39.73, -39.79) * mm});
            skLineSegment(sketch, "E672.MirrorCS", {"start": v(18.66, -50.97) * mm, "end": v(18.66, -53.71) * mm});
            skLineSegment(sketch, "E673.MirrorCS", {"start": v(37.17, -44.96) * mm, "end": v(38.74, -47.2) * mm});
            skLineSegment(sketch, "E674.MirrorCS", {"start": v(32.07, -52.13) * mm, "end": v(30.3, -50.03) * mm});
            skPoint(sketch, "E675.MirrorP", {"position": v(20.47, -54.46) * mm});
            skPoint(sketch, "E676.MirrorP", {"position": v(42.94, -41.65) * mm});
            skPoint(sketch, "E677.MirrorP", {"position": v(27.43, -54.14) * mm});
            skLineSegment(sketch, "E678.MirrorCS", {"start": v(15.65, -49.27) * mm, "end": v(13.97, -48.3) * mm});
            skLineSegment(sketch, "E679.MirrorCS", {"start": v(37.34, -48.6) * mm, "end": v(35.1, -47.04) * mm});
            skLineSegment(sketch, "E680.MirrorCS", {"start": v(30.44, -49.27) * mm, "end": v(32.12, -48.3) * mm});
            skPoint(sketch, "E681.MirrorP", {"position": v(12.15, -51.54) * mm});
            skLineSegment(sketch, "E682.MirrorCS", {"start": v(35.02, -46.26) * mm, "end": v(36.4, -44.89) * mm});
            skPoint(sketch, "E683.MirrorP", {"position": v(27.43, -50.37) * mm});
            skPoint(sketch, "E684.MirrorP", {"position": v(7.1, -47.55) * mm});
            skPoint(sketch, "E685.MirrorP", {"position": v(40.02, -39.26) * mm});
            skLineSegment(sketch, "E686.MirrorCS", {"start": v(20.61, -54.06) * mm, "end": v(21.55, -51.48) * mm});
            skPoint(sketch, "E687.MirrorP", {"position": v(1.09, -34.43) * mm});
            skLineSegment(sketch, "E688.MirrorCS", {"start": v(1.09, -34.43) * mm, "end": v(1.25, -36.27) * mm, "construction": true});
            skLineSegment(sketch, "E689.MirrorCS", {"start": v(14.02, -52.13) * mm, "end": v(15.78, -50.03) * mm});
            skPoint(sketch, "E690.MirrorP", {"position": v(13.75, -52.46) * mm});
            skPoint(sketch, "E691.MirrorP", {"position": v(21.76, -50.91) * mm});
            skLineSegment(sketch, "E692.MirrorCS", {"start": v(8.92, -44.96) * mm, "end": v(7.35, -47.2) * mm});
            skPoint(sketch, "E693.MirrorP", {"position": v(1.25, -36.27) * mm});
            skPoint(sketch, "E694.MirrorP", {"position": v(16.17, -49.57) * mm});
            skLineSegment(sketch, "E695.MirrorCS", {"start": v(21.16, -50.8) * mm, "end": v(19.25, -50.47) * mm});
            skPoint(sketch, "E696.MirrorP", {"position": v(38.99, -47.55) * mm});
            skPoint(sketch, "E697.MirrorP", {"position": v(33.94, -51.54) * mm});
            skPoint(sketch, "E698.MirrorP", {"position": v(13.44, -48) * mm});
            skPoint(sketch, "E699.MirrorP", {"position": v(24.33, -50.91) * mm});
            skPoint(sketch, "E700.MirrorP", {"position": v(18.66, -54.14) * mm});
            skLineSegment(sketch, "E701.MirrorCS", {"start": v(4.96, -36) * mm, "end": v(4.79, -34.06) * mm});
            skLineSegment(sketch, "E702.MirrorCS", {"start": v(25.47, -54.06) * mm, "end": v(24.54, -51.48) * mm});
            skPoint(sketch, "E703.MirrorP", {"position": v(41.35, -33.46) * mm});
            skPoint(sketch, "E704.MirrorP", {"position": v(4.73, -33.46) * mm});
            skPoint(sketch, "E705.MirrorP", {"position": v(32.65, -48) * mm});
            skLineSegment(sketch, "E706.MirrorCS", {"start": v(4.15, -33.61) * mm, "end": v(1.5, -34.32) * mm});
            skPoint(sketch, "E707.MirrorP", {"position": v(9.27, -44.46) * mm});
            skPoint(sketch, "E708.MirrorP", {"position": v(42.04, -43.25) * mm});
            skPoint(sketch, "E709.MirrorP", {"position": v(34.6, -46.69) * mm});
            skPoint(sketch, "E710.MirrorP", {"position": v(41.08, -36.6) * mm});
            skPoint(sketch, "E711.MirrorP", {"position": v(7.6, -42) * mm});
            skPoint(sketch, "E712.MirrorP", {"position": v(6.06, -39.26) * mm});
            skLineSegment(sketch, "E713.MirrorCS", {"start": v(11.06, -46.26) * mm, "end": v(9.7, -44.89) * mm});
            skLineSegment(sketch, "E714.MirrorCS", {"start": v(27.43, -50.97) * mm, "end": v(27.43, -53.71) * mm});
            skPoint(sketch, "E715.MirrorP", {"position": v(25.62, -54.46) * mm});
            skLineSegment(sketch, "E716.MirrorCS", {"start": v(18.66, -54.14) * mm, "end": v(20.47, -54.46) * mm, "construction": true});
            skPoint(sketch, "E717.MirrorP", {"position": v(11.5, -46.69) * mm});
            skPoint(sketch, "E718.MirrorP", {"position": v(36.82, -44.46) * mm});
            skLineSegment(sketch, "E719.MirrorCS", {"start": v(24.93, -50.8) * mm, "end": v(26.84, -50.47) * mm});
            skPoint(sketch, "E720.MirrorP", {"position": v(38.48, -42) * mm});
            skPoint(sketch, "E721.MirrorP", {"position": v(45, -34.43) * mm});
            skPoint(sketch, "E722.MirrorP", {"position": v(5, -36.6) * mm});
            skLineSegment(sketch, "E723.MirrorCS", {"start": v(4.45, -43.11) * mm, "end": v(7.04, -42.2) * mm});
            skPoint(sketch, "E724.MirrorP", {"position": v(29.92, -49.57) * mm});
            skPoint(sketch, "E725.MirrorP", {"position": v(8.4, -48.85) * mm});
            skLineSegment(sketch, "E726.MirrorCS", {"start": v(5.6, -39.64) * mm, "end": v(3.48, -41.38) * mm});
            skLineSegment(sketch, "E727.MirrorCS", {"start": v(7.31, -41.48) * mm, "end": v(6.36, -39.79) * mm});
            skPoint(sketch, "E728.MirrorP", {"position": v(3.15, -41.65) * mm});
            skLineSegment(sketch, "E729.MirrorCS", {"start": v(1.67, -36.3) * mm, "end": v(4.4, -36.54) * mm});
            skSolve(sketch);
        }
        {
            var Q0;
            Q0=qSketchRegion(id+"F0",true);
            extrude(context, id + "F2", {"entities" : qUnion([Q0]), "depth" : 6.35 * mm});
        }
        {
            var Q0;
            Q0=qSketchRegion(id+"F1",true);
            extrude(context, id + "F3", {"entities" : qUnion([Q0]), "depth" : 6.35 * mm});
        }
    });
